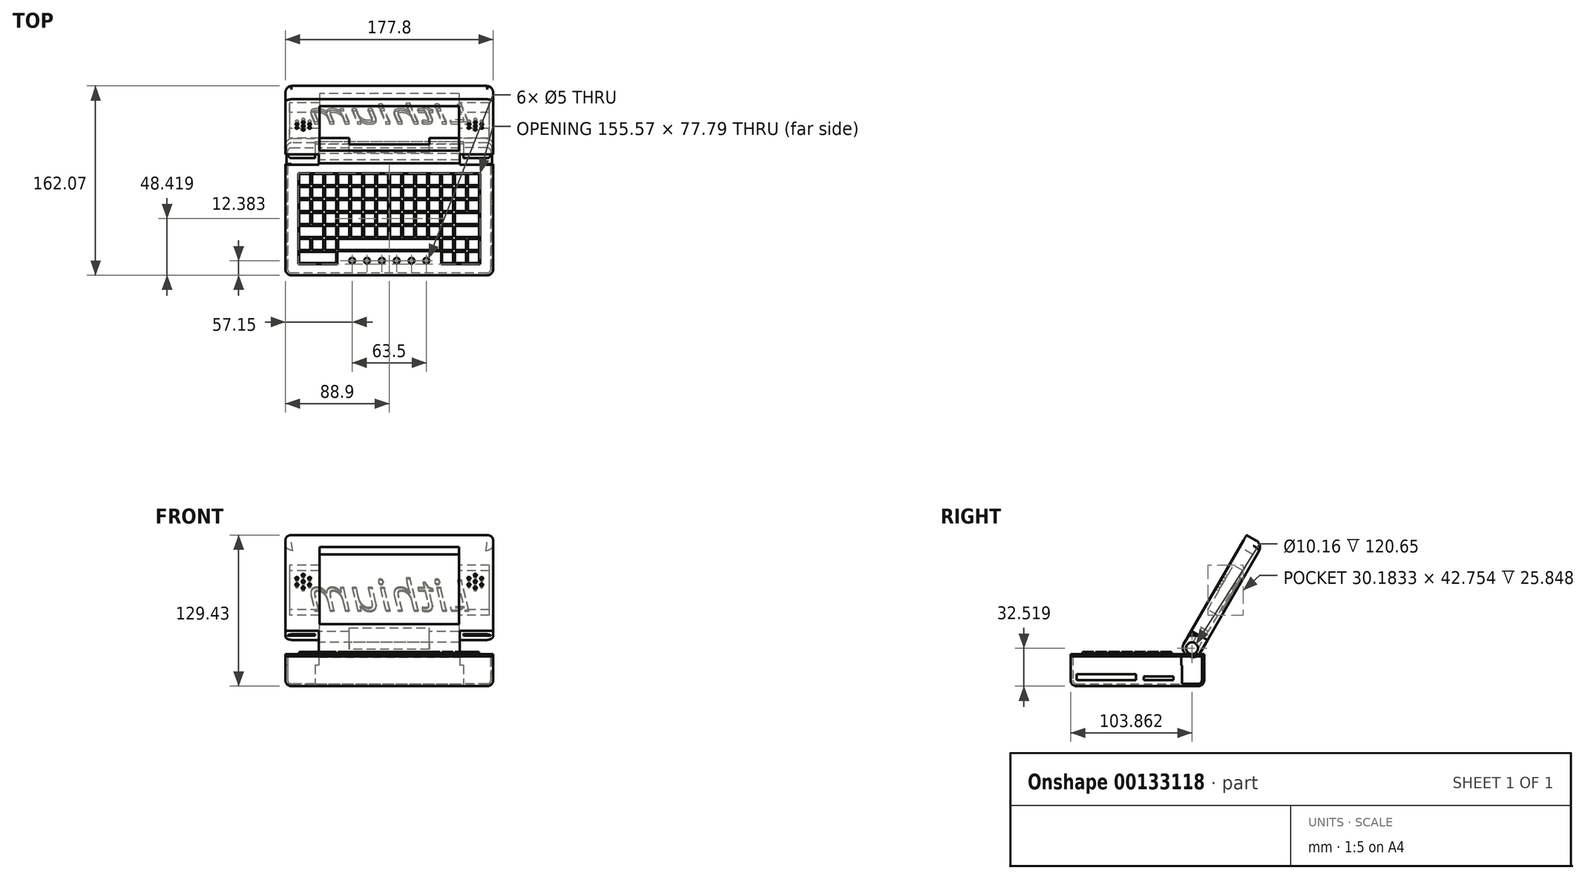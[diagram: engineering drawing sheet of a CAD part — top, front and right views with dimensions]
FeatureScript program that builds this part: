
annotation { "Feature Type Name" : "Feature", "Feature Type Description" : "" }
export const myFeature = defineFeature(function(context is Context, id is Id, definition is map)
    precondition{}
    {
        {
            var Q0;
            Q0=qCreatedBy(makeId("Top.planeOp"),FACE);
            var sketch = newSketch(context, id + "F0", { "sketchPlane" : qUnion([Q0])});
            skLineSegment(sketch, "E0.bottom", {"start": v(88.9, 57.15) * mm, "end": v(-88.9, 57.15) * mm});
            skLineSegment(sketch, "E0.top", {"start": v(88.9, -57.15) * mm, "end": v(-88.9, -57.15) * mm});
            skLineSegment(sketch, "E0.left", {"start": v(88.9, 57.15) * mm, "end": v(88.9, -57.15) * mm});
            skLineSegment(sketch, "E0.right", {"start": v(-88.9, 57.15) * mm, "end": v(-88.9, -57.15) * mm});
            skPoint(sketch, "E0.middle", {"position": v(0, 0) * mm});
            skSolve(sketch);
        }
        {
            var Q0;
            Q0 = qSketchRegion(id + "F0", true);
            extrude(context, id + "F1", {"entities" : qUnion([Q0]), "depth" : 25.4 * mm});
        }
        {
            var Q0;
            Q0=makeQuery(id+"F1.opExtrude","CAP_FACE",FACE,{"disambiguationData":[OSD([sQuery(id+"F0.wireOp",EDGE,"E0.bottom"),sQuery(id+"F0.wireOp",EDGE,"E0.top"),sQuery(id+"F0.wireOp",EDGE,"E0.left"),sQuery(id+"F0.wireOp",EDGE,"E0.right")])],"isStart":false});
            var sketch = newSketch(context, id + "F2", { "sketchPlane" : qUnion([Q0])});
            skLineSegment(sketch, "E1.bottom", {"start": v(-88.9, 57.15) * mm, "end": v(-63.5, 57.15) * mm});
            skLineSegment(sketch, "E1.top", {"start": v(-88.9, 38.1) * mm, "end": v(-63.5, 38.1) * mm});
            skLineSegment(sketch, "E1.left", {"start": v(-88.9, 57.15) * mm, "end": v(-88.9, 38.1) * mm});
            skLineSegment(sketch, "E1.right", {"start": v(-63.5, 57.15) * mm, "end": v(-63.5, 38.1) * mm});
            skLineSegment(sketch, "E2.MirrorCS", {"start": v(88.9, 57.15) * mm, "end": v(63.5, 57.15) * mm});
            skLineSegment(sketch, "E3.MirrorCS", {"start": v(88.9, 38.1) * mm, "end": v(63.5, 38.1) * mm});
            skLineSegment(sketch, "E4.MirrorCS", {"start": v(88.9, 57.15) * mm, "end": v(88.9, 38.1) * mm});
            skLineSegment(sketch, "E5.MirrorCS", {"start": v(63.5, 57.15) * mm, "end": v(63.5, 38.1) * mm});
            skSolve(sketch);
        }
        {
            var Q0;
            Q0 = qSketchRegion(id + "F2", true);
            extrude(context, id + "F3", {"entities" : qUnion([Q0]), "operationType" : NewBodyOperationType.ADD, "depth" : 19.05 * mm});
        }
        {
            var Q0;
            Q0=makeQuery(id+"F3.opExtrude","CAP_EDGE",EDGE,{"disambiguationData":[OSD([sQuery(id+"F2.wireOp",EDGE,"E3.MirrorCS")])],"isStart":false});
            var Q1;
            Q1=makeQuery(id+"F3.opExtrude","CAP_EDGE",EDGE,{"disambiguationData":[OSD([sQuery(id+"F2.wireOp",EDGE,"E2.MirrorCS")])],"isStart":false});
            var Q2;
            Q2=makeQuery(id+"F3.opExtrude","CAP_EDGE",EDGE,{"disambiguationData":[OSD([sQuery(id+"F2.wireOp",EDGE,"E1.bottom")])],"isStart":false});
            var Q3;
            Q3=makeQuery(id+"F3.opExtrude","CAP_EDGE",EDGE,{"disambiguationData":[OSD([sQuery(id+"F2.wireOp",EDGE,"E1.top")])],"isStart":false});
            fillet(context, id + "F4", {"entities" : qUnion([Q0, Q1, Q2, Q3]), "radius" : 9.52 * mm, "tangentPropagation" : true, "allowEdgeOverflow" : false});
        }
        {
            var Q0;
            Q0=makeQuery(id+"F4.opFillet","BLEND_EDGE",EDGE,{"blendedFrom":[makeQuery(id+"F3.opExtrude","CAP_EDGE",EDGE,{"disambiguationData":[OSD([sQuery(id+"F2.wireOp",EDGE,"E1.bottom")])],"isStart":false}),makeQuery(id+"F3.boolean.opBoolean","MERGE",FACE,{"derivedFrom":[makeQuery(id+"F1.opExtrude","SWEPT_FACE",FACE,{"disambiguationData":[OSD([sQuery(id+"F0.wireOp",EDGE,"E0.right")])]}),makeQuery(id+"F3.opExtrude","SWEPT_FACE",FACE,{"disambiguationData":[OSD([sQuery(id+"F2.wireOp",EDGE,"E1.left")])]})]})],"blendedInto":[makeQuery(id+"F3.boolean.opBoolean","MERGE",FACE,{"derivedFrom":[makeQuery(id+"F1.opExtrude","SWEPT_FACE",FACE,{"disambiguationData":[OSD([sQuery(id+"F0.wireOp",EDGE,"E0.right")])]}),makeQuery(id+"F3.opExtrude","SWEPT_FACE",FACE,{"disambiguationData":[OSD([sQuery(id+"F2.wireOp",EDGE,"E1.left")])]})]})]});
            var Q1;
            Q1=makeQuery(id+"F3.opExtrude","SWEPT_EDGE",EDGE,{"disambiguationData":[OSD([sQuery(id+"F0.wireOp",EDGE,"E0.right"),sQuery(id+"F2.wireOp",EDGE,"E1.top"),sQuery(id+"F2.wireOp",EDGE,"E1.left")])]});
            var Q2;
            Q2=makeQuery(id+"F1.opExtrude","SWEPT_EDGE",EDGE,{"disambiguationData":[OSD([sQuery(id+"F0.wireOp",EDGE,"E0.top"),sQuery(id+"F0.wireOp",EDGE,"E0.right")])]});
            var Q3;
            Q3=makeQuery(id+"F3.boolean.opBoolean","MERGE",EDGE,{"derivedFrom":[makeQuery(id+"F1.opExtrude","SWEPT_EDGE",EDGE,{"disambiguationData":[OSD([sQuery(id+"F0.wireOp",EDGE,"E0.bottom"),sQuery(id+"F0.wireOp",EDGE,"E0.right")])]}),makeQuery(id+"F3.opExtrude","SWEPT_EDGE",EDGE,{"disambiguationData":[OSD([sQuery(id+"F2.wireOp",EDGE,"E1.bottom"),sQuery(id+"F2.wireOp",EDGE,"E1.left")])]})]});
            var Q4;
            Q4=makeQuery(id+"F1.opExtrude","SWEPT_EDGE",EDGE,{"disambiguationData":[OSD([sQuery(id+"F0.wireOp",EDGE,"E0.top"),sQuery(id+"F0.wireOp",EDGE,"E0.left")])]});
            var Q5;
            Q5=makeQuery(id+"F3.boolean.opBoolean","MERGE",EDGE,{"derivedFrom":[makeQuery(id+"F1.opExtrude","SWEPT_EDGE",EDGE,{"disambiguationData":[OSD([sQuery(id+"F0.wireOp",EDGE,"E0.bottom"),sQuery(id+"F0.wireOp",EDGE,"E0.left")])]}),makeQuery(id+"F3.opExtrude","SWEPT_EDGE",EDGE,{"disambiguationData":[OSD([sQuery(id+"F2.wireOp",EDGE,"E2.MirrorCS"),sQuery(id+"F2.wireOp",EDGE,"E4.MirrorCS")])]})]});
            var Q6;
            Q6=makeQuery(id+"F1.opExtrude","CAP_FACE",FACE,{"disambiguationData":[OSD([sQuery(id+"F0.wireOp",EDGE,"E0.bottom"),sQuery(id+"F0.wireOp",EDGE,"E0.top"),sQuery(id+"F0.wireOp",EDGE,"E0.left"),sQuery(id+"F0.wireOp",EDGE,"E0.right")])],"isStart":true});
            fillet(context, id + "F5", {"entities" : qUnion([Q0, Q1, Q2, Q3, Q4, Q5, Q6]), "radius" : 5.08 * mm, "tangentPropagation" : true, "allowEdgeOverflow" : false});
        }
        {
            var Q0;
            Q0=makeQuery(id+"F1.opExtrude","CAP_FACE",FACE,{"disambiguationData":[OSD([sQuery(id+"F0.wireOp",EDGE,"E0.bottom"),sQuery(id+"F0.wireOp",EDGE,"E0.top"),sQuery(id+"F0.wireOp",EDGE,"E0.left"),sQuery(id+"F0.wireOp",EDGE,"E0.right")])],"isStart":false});
            shell(context, id + "F6", {"entities" : qUnion([Q0]), "thickness" : 2 * mm});
        }
        {
            var Q0;
            Q0=makeQuery(id+"F3.opExtrude","SWEPT_FACE",FACE,{"disambiguationData":[OSD([sQuery(id+"F2.wireOp",EDGE,"E5.MirrorCS")])]});
            var sketch = newSketch(context, id + "F7", { "sketchPlane" : qUnion([Q0])});
            skCircle(sketch, "E6", {"center": v(-47.63, 34.93) * mm, "radius": 7.94 * mm});
            skSolve(sketch);
        }
        {
            var Q0;
            Q0 = qSketchRegion(id + "F7", true);
            extrude(context, id + "F8", {"entities" : qUnion([Q0]), "operationType" : NewBodyOperationType.REMOVE, "oppositeDirection" : true, "depth" : 6.35 * mm});
        }
        {
            var Q0;
            Q0=makeQuery(id+"F3.opExtrude","SWEPT_FACE",FACE,{"disambiguationData":[OSD([sQuery(id+"F2.wireOp",EDGE,"E1.right")])]});
            var sketch = newSketch(context, id + "F9", { "sketchPlane" : qUnion([Q0])});
            skCircle(sketch, "E7", {"center": v(47.63, 34.93) * mm, "radius": 7.94 * mm});
            skSolve(sketch);
        }
        {
            var Q0;
            Q0 = qSketchRegion(id + "F9", true);
            extrude(context, id + "F10", {"entities" : qUnion([Q0]), "operationType" : NewBodyOperationType.REMOVE, "oppositeDirection" : true, "depth" : 6.35 * mm});
        }
        {
            var Q0;
            {var subQ0=sQuery(id+"F0.wireOp",EDGE,"E0.right");var subQ1=sQuery(id+"F0.wireOp",EDGE,"E0.left");var subQ2=sQuery(id+"F0.wireOp",EDGE,"E0.top");var subQ3=sQuery(id+"F0.wireOp",EDGE,"E0.bottom");Q0=makeQuery(id+"F6.opShell","OFFSET_FACE",FACE,{"disambiguationData":[OSD([subQ3,subQ2,subQ1,subQ0]),TDD([makeQuery(id+"F1.opExtrude","CAP_FACE",FACE,{"disambiguationData":[OSD([subQ3,subQ2,subQ1,subQ0])],"isStart":false})]),OD(0.0)]});}
            var sketch = newSketch(context, id + "F11", { "sketchPlane" : qUnion([Q0])});
            skLineSegment(sketch, "E8.bottom", {"start": v(-83.82, -57.15) * mm, "end": v(83.82, -57.15) * mm});
            skLineSegment(sketch, "E8.top", {"start": v(-88.9, 57.15) * mm, "end": v(88.9, 57.15) * mm});
            skLineSegment(sketch, "E8.left", {"start": v(-88.9, -52.07) * mm, "end": v(-88.9, 57.15) * mm});
            skLineSegment(sketch, "E8.right", {"start": v(88.9, -52.07) * mm, "end": v(88.9, 57.15) * mm});
            skPoint(sketch, "E9.visualSharp", {"position": v(-88.9, -57.15) * mm});
            skArc(sketch, "E9.filletArc", {"start": v(-88.9, -52.07) * mm, "mid": v(-87.41, -55.66) * mm, "end": v(-83.82, -57.15) * mm});
            skPoint(sketch, "E10.visualSharp", {"position": v(88.9, -57.15) * mm});
            skArc(sketch, "E10.filletArc", {"start": v(83.82, -57.15) * mm, "mid": v(87.41, -55.66) * mm, "end": v(88.9, -52.07) * mm});
            skLineSegment(sketch, "E11.top", {"start": v(-88.9, 38.1) * mm, "end": v(-63.5, 38.1) * mm});
            skLineSegment(sketch, "E11.right", {"start": v(-63.5, 57.15) * mm, "end": v(-63.5, 38.1) * mm});
            skLineSegment(sketch, "E12.MirrorCS", {"start": v(63.5, 57.15) * mm, "end": v(63.5, 38.1) * mm});
            skLineSegment(sketch, "E13.MirrorCS", {"start": v(88.9, 57.15) * mm, "end": v(88.9, 38.1) * mm});
            skLineSegment(sketch, "E14.MirrorCS", {"start": v(88.9, 38.1) * mm, "end": v(63.5, 38.1) * mm});
            skLineSegment(sketch, "E15.MirrorCS", {"start": v(88.9, 57.15) * mm, "end": v(63.5, 57.15) * mm});
            skSolve(sketch);
        }
        {
            var Q0;
            Q0 = qSketchRegion(id + "F11", true);
            extrude(context, id + "F12", {"entities" : qUnion([Q0]), "depth" : 2 * mm});
        }
        {
            var Q0;
            Q0=makeQuery(id+"F12.opExtrude","CAP_FACE",FACE,{"disambiguationData":[OSD([sQuery(id+"F11.wireOp",EDGE,"E8.bottom"),sQuery(id+"F11.wireOp",EDGE,"E8.top"),sQuery(id+"F11.wireOp",EDGE,"E8.left"),sQuery(id+"F11.wireOp",EDGE,"E8.right"),sQuery(id+"F11.wireOp",EDGE,"E9.filletArc"),sQuery(id+"F11.wireOp",EDGE,"E10.filletArc"),sQuery(id+"F11.wireOp",EDGE,"E13.MirrorCS"),sQuery(id+"F11.wireOp",EDGE,"E15.MirrorCS")])],"isStart":false});
            var sketch = newSketch(context, id + "F13", { "sketchPlane" : qUnion([Q0])});
            skLineSegment(sketch, "E16.bottom", {"start": v(-88.9, 57.15) * mm, "end": v(-63.5, 57.15) * mm});
            skLineSegment(sketch, "E16.top", {"start": v(-88.9, 38.1) * mm, "end": v(-63.5, 38.1) * mm});
            skLineSegment(sketch, "E16.left", {"start": v(-88.9, 57.15) * mm, "end": v(-88.9, 38.1) * mm});
            skLineSegment(sketch, "E16.right", {"start": v(-63.5, 57.15) * mm, "end": v(-63.5, 38.1) * mm});
            skLineSegment(sketch, "E17.MirrorCS", {"start": v(63.5, 57.15) * mm, "end": v(63.5, 38.1) * mm});
            skLineSegment(sketch, "E18.MirrorCS", {"start": v(88.9, 57.15) * mm, "end": v(88.9, 38.1) * mm});
            skLineSegment(sketch, "E19.MirrorCS", {"start": v(88.9, 38.1) * mm, "end": v(63.5, 38.1) * mm});
            skLineSegment(sketch, "E20.MirrorCS", {"start": v(88.9, 57.15) * mm, "end": v(63.5, 57.15) * mm});
            skSolve(sketch);
        }
        {
            var Q0;
            Q0 = qSketchRegion(id + "F13", true);
            extrude(context, id + "F14", {"entities" : qUnion([Q0]), "operationType" : NewBodyOperationType.REMOVE, "oppositeDirection" : true, "depth" : 25.4 * mm});
        }
        {
            var Q0;
            Q0=makeQuery(id+"F12.opExtrude","CAP_FACE",FACE,{"disambiguationData":[OSD([sQuery(id+"F11.wireOp",EDGE,"E8.bottom"),sQuery(id+"F11.wireOp",EDGE,"E8.top"),sQuery(id+"F11.wireOp",EDGE,"E8.left"),sQuery(id+"F11.wireOp",EDGE,"E8.right"),sQuery(id+"F11.wireOp",EDGE,"E9.filletArc"),sQuery(id+"F11.wireOp",EDGE,"E10.filletArc"),sQuery(id+"F11.wireOp",EDGE,"E13.MirrorCS"),sQuery(id+"F11.wireOp",EDGE,"E15.MirrorCS")])],"isStart":false});
            var sketch = newSketch(context, id + "F15", { "sketchPlane" : qUnion([Q0])});
            skLineSegment(sketch, "E21.bottom", {"start": v(-83.82, -57.15) * mm, "end": v(83.82, -57.15) * mm});
            skLineSegment(sketch, "E21.top", {"start": v(-88.9, 57.15) * mm, "end": v(88.9, 57.15) * mm});
            skLineSegment(sketch, "E21.left", {"start": v(-88.9, -52.07) * mm, "end": v(-88.9, 57.15) * mm});
            skLineSegment(sketch, "E21.right", {"start": v(88.9, -52.07) * mm, "end": v(88.9, 57.15) * mm});
            skPoint(sketch, "E22.visualSharp", {"position": v(-88.9, -57.15) * mm});
            skArc(sketch, "E22.filletArc", {"start": v(-88.9, -52.07) * mm, "mid": v(-87.41, -55.66) * mm, "end": v(-83.82, -57.15) * mm});
            skPoint(sketch, "E23.visualSharp", {"position": v(88.9, -57.15) * mm});
            skArc(sketch, "E23.filletArc", {"start": v(83.82, -57.15) * mm, "mid": v(87.41, -55.66) * mm, "end": v(88.9, -52.07) * mm});
            skSolve(sketch);
        }
        {
            var Q0;
            Q0 = qSketchRegion(id + "F15", true);
            extrude(context, id + "F16", {"entities" : qUnion([Q0]), "depth" : 15.88 * mm});
        }
        {
            var Q0;
            Q0=makeQuery(id+"F16.opExtrude","CAP_FACE",FACE,{"disambiguationData":[OSD([sQuery(id+"F15.wireOp",EDGE,"E21.bottom"),sQuery(id+"F15.wireOp",EDGE,"E21.top"),sQuery(id+"F15.wireOp",EDGE,"E21.left"),sQuery(id+"F15.wireOp",EDGE,"E21.right"),sQuery(id+"F15.wireOp",EDGE,"E22.filletArc"),sQuery(id+"F15.wireOp",EDGE,"E23.filletArc")])],"isStart":false});
            var sketch = newSketch(context, id + "F17", { "sketchPlane" : qUnion([Q0])});
            skLineSegment(sketch, "E24.bottom", {"start": v(-88.9, 57.15) * mm, "end": v(-60.32, 57.15) * mm});
            skLineSegment(sketch, "E24.top", {"start": v(-88.9, 37.46) * mm, "end": v(-60.32, 37.46) * mm});
            skLineSegment(sketch, "E24.left", {"start": v(-88.9, 57.15) * mm, "end": v(-88.9, 37.46) * mm});
            skLineSegment(sketch, "E24.right", {"start": v(-60.32, 57.15) * mm, "end": v(-60.32, 37.46) * mm});
            skLineSegment(sketch, "E25.MirrorCS", {"start": v(60.32, 57.15) * mm, "end": v(60.32, 37.46) * mm});
            skLineSegment(sketch, "E26.MirrorCS", {"start": v(88.9, 57.15) * mm, "end": v(88.9, 37.46) * mm});
            skLineSegment(sketch, "E27.MirrorCS", {"start": v(88.9, 37.46) * mm, "end": v(60.32, 37.46) * mm});
            skLineSegment(sketch, "E28.MirrorCS", {"start": v(88.9, 57.15) * mm, "end": v(60.32, 57.15) * mm});
            skSolve(sketch);
        }
        {
            var Q0;
            Q0 = qSketchRegion(id + "F17", true);
            extrude(context, id + "F18", {"entities" : qUnion([Q0]), "operationType" : NewBodyOperationType.REMOVE, "oppositeDirection" : true, "depth" : 25.4 * mm});
        }
        {
            var Q0;
            Q0=makeQuery(id+"F16.opExtrude","CAP_EDGE",EDGE,{"disambiguationData":[OSD([sQuery(id+"F15.wireOp",EDGE,"E21.top")])],"isStart":true});
            var Q1;
            Q1=makeQuery(id+"F16.opExtrude","CAP_EDGE",EDGE,{"disambiguationData":[OSD([sQuery(id+"F15.wireOp",EDGE,"E21.top")])],"isStart":false});
            var Q2;
            Q2=makeQuery(id+"F18.boolean.opBoolean","COPY",EDGE,{"derivedFrom":makeQuery(id+"F18.opExtrude","CAP_EDGE",EDGE,{"disambiguationData":[OSD([sQuery(id+"F17.wireOp",EDGE,"E27.MirrorCS")])],"isStart":true})});
            var Q3;
            Q3=makeQuery(id+"F16.opExtrude","CAP_EDGE",EDGE,{"disambiguationData":[OSD([sQuery(id+"F15.wireOp",EDGE,"E21.right")])],"isStart":false});
            var Q4;
            Q4=makeQuery(id+"F16.opExtrude","CAP_EDGE",EDGE,{"disambiguationData":[OSD([sQuery(id+"F15.wireOp",EDGE,"E23.filletArc")])],"isStart":false});
            var Q5;
            Q5=makeQuery(id+"F16.opExtrude","CAP_EDGE",EDGE,{"disambiguationData":[OSD([sQuery(id+"F15.wireOp",EDGE,"E21.bottom")])],"isStart":false});
            var Q6;
            Q6=makeQuery(id+"F16.opExtrude","CAP_EDGE",EDGE,{"disambiguationData":[OSD([sQuery(id+"F15.wireOp",EDGE,"E22.filletArc")])],"isStart":false});
            var Q7;
            Q7=makeQuery(id+"F16.opExtrude","CAP_EDGE",EDGE,{"disambiguationData":[OSD([sQuery(id+"F15.wireOp",EDGE,"E21.left")])],"isStart":false});
            var Q8;
            Q8=makeQuery(id+"F18.boolean.opBoolean","COPY",EDGE,{"derivedFrom":makeQuery(id+"F18.opExtrude","CAP_EDGE",EDGE,{"disambiguationData":[OSD([sQuery(id+"F17.wireOp",EDGE,"E24.top")])],"isStart":true})});
            fillet(context, id + "F19", {"entities" : qUnion([Q0, Q1, Q2, Q3, Q4, Q5, Q6, Q7, Q8]), "radius" : 6.35 * mm, "tangentPropagation" : true, "allowEdgeOverflow" : false});
        }
        {
            var Q0;
            Q0=qCreatedBy(makeId("Top.planeOp"),FACE);
            cPlane(context, id + "F20", {"entities" : qUnion([Q0]), "cplaneType" : CPlaneType.OFFSET, "offset" : 34.92 * mm, "width" : 152.4 * mm, "height" : 152.4 * mm});
        }
        {
            var Q0;
            Q0=qCreatedBy(id+"F20.planeOp",FACE);
            var sketch = newSketch(context, id + "F21", { "sketchPlane" : qUnion([Q0])});
            skLineSegment(sketch, "E29", {"start": v(-88.65, 47.63) * mm, "end": v(89.15, 47.63) * mm});
            skSolve(sketch);
        }
        {
            var Q0;
            Q0=makeQuery(id+"F12.opExtrude","CAP_FACE",FACE,{"disambiguationData":[OSD([sQuery(id+"F11.wireOp",EDGE,"E8.bottom"),sQuery(id+"F11.wireOp",EDGE,"E8.top"),sQuery(id+"F11.wireOp",EDGE,"E8.left"),sQuery(id+"F11.wireOp",EDGE,"E8.right"),sQuery(id+"F11.wireOp",EDGE,"E9.filletArc"),sQuery(id+"F11.wireOp",EDGE,"E10.filletArc"),sQuery(id+"F11.wireOp",EDGE,"E13.MirrorCS"),sQuery(id+"F11.wireOp",EDGE,"E15.MirrorCS")])],"isStart":false});
            var sketch = newSketch(context, id + "F22", { "sketchPlane" : qUnion([Q0])});
            skLineSegment(sketch, "E30.bottom", {"start": v(77.79, 30.16) * mm, "end": v(-77.79, 30.16) * mm});
            skLineSegment(sketch, "E30.top", {"start": v(77.79, -36.51) * mm, "end": v(-77.79, -36.51) * mm});
            skLineSegment(sketch, "E30.left", {"start": v(77.79, 30.16) * mm, "end": v(77.79, -36.51) * mm});
            skLineSegment(sketch, "E30.right", {"start": v(-77.79, 30.16) * mm, "end": v(-77.79, -36.51) * mm});
            skPoint(sketch, "E30.middle", {"position": v(0, -3.18) * mm});
            skLineSegment(sketch, "E31.bottom", {"start": v(77.79, -36.51) * mm, "end": v(44.45, -36.51) * mm});
            skLineSegment(sketch, "E31.top", {"start": v(77.79, -47.62) * mm, "end": v(44.45, -47.63) * mm});
            skLineSegment(sketch, "E31.left", {"start": v(77.79, -36.51) * mm, "end": v(77.79, -47.62) * mm});
            skLineSegment(sketch, "E31.right", {"start": v(44.45, -36.51) * mm, "end": v(44.45, -47.63) * mm});
            skLineSegment(sketch, "E32.MirrorCS", {"start": v(-77.79, -36.51) * mm, "end": v(-44.45, -36.51) * mm});
            skLineSegment(sketch, "E33.MirrorCS", {"start": v(-77.79, -47.62) * mm, "end": v(-44.45, -47.63) * mm});
            skLineSegment(sketch, "E34.MirrorCS", {"start": v(-44.45, -36.51) * mm, "end": v(-44.45, -47.63) * mm});
            skLineSegment(sketch, "E35.MirrorCS", {"start": v(-77.79, -36.51) * mm, "end": v(-77.79, -47.62) * mm});
            skSolve(sketch);
        }
        {
            var Q0;
            Q0 = qSketchRegion(id + "F22", true);
            extrude(context, id + "F23", {"entities" : qUnion([Q0]), "operationType" : NewBodyOperationType.REMOVE, "oppositeDirection" : true, "depth" : 25.4 * mm});
        }
        {
            var Q0;
            Q0=makeQuery(id+"F16.opExtrude","CAP_FACE",FACE,{"disambiguationData":[OSD([sQuery(id+"F15.wireOp",EDGE,"E21.bottom"),sQuery(id+"F15.wireOp",EDGE,"E21.top"),sQuery(id+"F15.wireOp",EDGE,"E21.left"),sQuery(id+"F15.wireOp",EDGE,"E21.right"),sQuery(id+"F15.wireOp",EDGE,"E22.filletArc"),sQuery(id+"F15.wireOp",EDGE,"E23.filletArc")])],"isStart":true});
            var sketch = newSketch(context, id + "F24", { "sketchPlane" : qUnion([Q0])});
            skLineSegment(sketch, "E36.bottom", {"start": v(59.7, 45.27) * mm, "end": v(-59.7, 45.27) * mm});
            skLineSegment(sketch, "E36.top", {"start": v(59.7, -30.93) * mm, "end": v(-59.69, -30.93) * mm});
            skLineSegment(sketch, "E36.left", {"start": v(59.7, 45.27) * mm, "end": v(59.7, -30.93) * mm});
            skLineSegment(sketch, "E36.right", {"start": v(-59.7, 45.27) * mm, "end": v(-59.69, -30.93) * mm});
            skPoint(sketch, "E36.middle", {"position": v(0, 7.17) * mm});
            skSolve(sketch);
        }
        {
            var Q0;
            Q0 = qSketchRegion(id + "F24", true);
            extrude(context, id + "F25", {"entities" : qUnion([Q0]), "operationType" : NewBodyOperationType.REMOVE, "oppositeDirection" : true, "depth" : 12.7 * mm});
        }
        {
            var Q0;
            Q0=makeQuery(id+"F16.opExtrude","SWEPT_BODY",BODY,{"disambiguationData":[OSD([sQuery(id+"F15.wireOp",EDGE,"E21.bottom"),sQuery(id+"F15.wireOp",EDGE,"E21.top"),sQuery(id+"F15.wireOp",EDGE,"E21.left"),sQuery(id+"F15.wireOp",EDGE,"E21.right"),sQuery(id+"F15.wireOp",EDGE,"E22.filletArc"),sQuery(id+"F15.wireOp",EDGE,"E23.filletArc")])]});
            var Q1;
            Q1=sQuery(id+"F21.wireOp",EDGE,"E29");
            transform(context, id + "F26", {"entities" : qUnion([Q0]), "transformType" : TransformType.ROTATION, "transformAxis" : qUnion([Q1]), "angle" : 90 * degree, "oppositeDirection" : true, "makeCopy" : false});
        }
        {
            var Q0;
            Q0=makeQuery(id+"F25.boolean.opBoolean","COPY",FACE,{"derivedFrom":makeQuery(id+"F25.opExtrude","CAP_FACE",FACE,{"disambiguationData":[OSD([sQuery(id+"F24.wireOp",EDGE,"E36.bottom"),sQuery(id+"F24.wireOp",EDGE,"E36.top"),sQuery(id+"F24.wireOp",EDGE,"E36.left"),sQuery(id+"F24.wireOp",EDGE,"E36.right")])],"isStart":false})});
            var sketch = newSketch(context, id + "F27", { "sketchPlane" : qUnion([Q0])});
            skLineSegment(sketch, "E37.bottom", {"start": v(85.54, 111.66) * mm, "end": v(-85.54, 111.66) * mm});
            skLineSegment(sketch, "E37.top", {"start": v(85.54, 67.79) * mm, "end": v(-85.54, 67.79) * mm});
            skLineSegment(sketch, "E37.left", {"start": v(85.54, 111.66) * mm, "end": v(85.54, 67.79) * mm});
            skLineSegment(sketch, "E37.right", {"start": v(-85.54, 111.66) * mm, "end": v(-85.54, 67.79) * mm});
            skPoint(sketch, "E37.middle", {"position": v(0, 89.72) * mm});
            skPoint(sketch, "E37.middle.positionSnap0", {"position": v(-59.7, 89.72) * mm});
            skPoint(sketch, "E37.middle.positionSnap1", {"position": v(0, 127.82) * mm});
            skPoint(sketch, "E37.centerSnap0", {"position": v(-59.7, 89.72) * mm});
            skPoint(sketch, "E37.centerSnap1", {"position": v(0, 127.82) * mm});
            skSolve(sketch);
        }
        {
            var Q0;
            Q0 = qSketchRegion(id + "F27", true);
            extrude(context, id + "F28", {"entities" : qUnion([Q0]), "operationType" : NewBodyOperationType.REMOVE, "depth" : 9.52 * mm});
        }
        {
            var Q0;
            Q0=makeQuery(id+"F16.opExtrude","CAP_FACE",FACE,{"disambiguationData":[OSD([sQuery(id+"F15.wireOp",EDGE,"E21.bottom"),sQuery(id+"F15.wireOp",EDGE,"E21.top"),sQuery(id+"F15.wireOp",EDGE,"E21.left"),sQuery(id+"F15.wireOp",EDGE,"E21.right"),sQuery(id+"F15.wireOp",EDGE,"E22.filletArc"),sQuery(id+"F15.wireOp",EDGE,"E23.filletArc")])],"isStart":true});
            var sketch = newSketch(context, id + "F29", { "sketchPlane" : qUnion([Q0])});
            skCircle(sketch, "E38", {"center": v(-73.63, 93.85) * mm, "radius": 1.27 * mm});
            skCircle(sketch, "E39", {"center": v(-73.63, 100.14) * mm, "radius": 1.27 * mm});
            skCircle(sketch, "E40.1.0", {"center": v(-79.08, 97) * mm, "radius": 1.27 * mm});
            skCircle(sketch, "E40.2.0", {"center": v(-79.08, 90.7) * mm, "radius": 1.27 * mm});
            skCircle(sketch, "E40.3.0", {"center": v(-73.63, 87.55) * mm, "radius": 1.27 * mm});
            skCircle(sketch, "E40.4.0", {"center": v(-68.17, 90.7) * mm, "radius": 1.27 * mm});
            skCircle(sketch, "E40.5.0", {"center": v(-68.17, 97) * mm, "radius": 1.27 * mm});
            skCircle(sketch, "E41.MirrorC", {"center": v(73.63, 93.85) * mm, "radius": 1.27 * mm});
            skCircle(sketch, "E42.MirrorC", {"center": v(73.63, 100.14) * mm, "radius": 1.27 * mm});
            skCircle(sketch, "E43.MirrorC", {"center": v(68.17, 97) * mm, "radius": 1.27 * mm});
            skCircle(sketch, "E44.MirrorC", {"center": v(79.08, 97) * mm, "radius": 1.27 * mm});
            skCircle(sketch, "E45.MirrorC", {"center": v(79.08, 90.7) * mm, "radius": 1.27 * mm});
            skCircle(sketch, "E46.MirrorC", {"center": v(68.17, 90.7) * mm, "radius": 1.27 * mm});
            skCircle(sketch, "E47.MirrorC", {"center": v(73.63, 87.55) * mm, "radius": 1.27 * mm});
            skSolve(sketch);
        }
        {
            var Q0;
            Q0 = qSketchRegion(id + "F29", true);
            extrude(context, id + "F30", {"entities" : qUnion([Q0]), "operationType" : NewBodyOperationType.REMOVE, "oppositeDirection" : true, "depth" : 12.7 * mm});
        }
        {
            var Q0;
            Q0=makeQuery(id+"F18.boolean.opBoolean","COPY",FACE,{"derivedFrom":makeQuery(id+"F18.opExtrude","SWEPT_FACE",FACE,{"disambiguationData":[OSD([sQuery(id+"F17.wireOp",EDGE,"E24.right")])]})});
            var sketch = newSketch(context, id + "F31", { "sketchPlane" : qUnion([Q0])});
            skCircle(sketch, "E48", {"center": v(-48.04, 32.39) * mm, "radius": 5.08 * mm});
            skPoint(sketch, "E48.centerSnap0", {"position": v(-48.04, 25.4) * mm});
            skSolve(sketch);
        }
        {
            var Q0;
            Q0 = qSketchRegion(id + "F31", true);
            extrude(context, id + "F32", {"entities" : qUnion([Q0]), "operationType" : NewBodyOperationType.REMOVE, "oppositeDirection" : true, "depth" : 203.2 * mm});
        }
        {
            var Q0;
            Q0=makeQuery(id+"F25.boolean.opBoolean","COPY",FACE,{"derivedFrom":makeQuery(id+"F25.opExtrude","SWEPT_FACE",FACE,{"disambiguationData":[OSD([sQuery(id+"F24.wireOp",EDGE,"E36.top")])]})});
            var sketch = newSketch(context, id + "F33", { "sketchPlane" : qUnion([Q0])});
            skLineSegment(sketch, "E49.bottom", {"start": v(-34.3, 52.8) * mm, "end": v(34.3, 52.8) * mm});
            skLineSegment(sketch, "E49.top", {"start": v(-34.3, 46.45) * mm, "end": v(34.3, 46.45) * mm});
            skLineSegment(sketch, "E49.left", {"start": v(-34.3, 52.8) * mm, "end": v(-34.3, 46.45) * mm});
            skLineSegment(sketch, "E49.right", {"start": v(34.3, 52.8) * mm, "end": v(34.3, 46.45) * mm});
            skSolve(sketch);
        }
        {
            var Q0;
            Q0 = qSketchRegion(id + "F33", true);
            extrude(context, id + "F34", {"entities" : qUnion([Q0]), "operationType" : NewBodyOperationType.REMOVE, "oppositeDirection" : true, "depth" : 19.05 * mm});
        }
        {
            var Q0;
            Q0=makeQuery(id+"F16.opExtrude","CAP_FACE",FACE,{"disambiguationData":[OSD([sQuery(id+"F15.wireOp",EDGE,"E21.bottom"),sQuery(id+"F15.wireOp",EDGE,"E21.top"),sQuery(id+"F15.wireOp",EDGE,"E21.left"),sQuery(id+"F15.wireOp",EDGE,"E21.right"),sQuery(id+"F15.wireOp",EDGE,"E22.filletArc"),sQuery(id+"F15.wireOp",EDGE,"E23.filletArc")])],"isStart":false});
            var sketch = newSketch(context, id + "F35", { "sketchPlane" : qUnion([Q0])});
            skText(sketch, "E50", { "text": "Lithium", "fontName": "OpenSans-Italic.ttf"});
            const initialGuessF35  = {"E50": [-0.06985, 0.07356, 1, 0, 0.0301]};
            skSetInitialGuess(sketch, initialGuessF35);
            skSolve(sketch);
        }
        {
            var Q0;
            Q0 = qSketchRegion(id + "F35", true);
            extrude(context, id + "F36", {"entities" : qUnion([Q0]), "operationType" : NewBodyOperationType.REMOVE, "oppositeDirection" : true, "depth" : 2 * mm});
        }
        {
            var Q0;
            Q0=makeQuery(id+"F16.opExtrude","SWEPT_BODY",BODY,{"disambiguationData":[OSD([sQuery(id+"F15.wireOp",EDGE,"E21.bottom"),sQuery(id+"F15.wireOp",EDGE,"E21.top"),sQuery(id+"F15.wireOp",EDGE,"E21.left"),sQuery(id+"F15.wireOp",EDGE,"E21.right"),sQuery(id+"F15.wireOp",EDGE,"E22.filletArc"),sQuery(id+"F15.wireOp",EDGE,"E23.filletArc")])]});
            var Q1;
            Q1=sQuery(id+"F21.wireOp",EDGE,"E29");
            transform(context, id + "F37", {"entities" : qUnion([Q0]), "transformType" : TransformType.ROTATION, "transformAxis" : qUnion([Q1]), "angle" : 30 * degree, "oppositeDirection" : true, "makeCopy" : false});
        }
        {
            var Q0;
            Q0=makeQuery(id+"F12.opExtrude","CAP_FACE",FACE,{"disambiguationData":[OSD([sQuery(id+"F11.wireOp",EDGE,"E8.bottom"),sQuery(id+"F11.wireOp",EDGE,"E8.top"),sQuery(id+"F11.wireOp",EDGE,"E8.left"),sQuery(id+"F11.wireOp",EDGE,"E8.right"),sQuery(id+"F11.wireOp",EDGE,"E9.filletArc"),sQuery(id+"F11.wireOp",EDGE,"E10.filletArc"),sQuery(id+"F11.wireOp",EDGE,"E13.MirrorCS"),sQuery(id+"F11.wireOp",EDGE,"E15.MirrorCS")])],"isStart":false});
            var sketch = newSketch(context, id + "F38", { "sketchPlane" : qUnion([Q0])});
            skCircle(sketch, "E51", {"center": v(-31.75, -44.77) * mm, "radius": 2.5 * mm});
            skCircle(sketch, "E52.1.0.0", {"center": v(-19.05, -44.77) * mm, "radius": 2.5 * mm});
            skCircle(sketch, "E52.2.0.0", {"center": v(-6.35, -44.77) * mm, "radius": 2.5 * mm});
            skCircle(sketch, "E52.3.0.0", {"center": v(6.35, -44.77) * mm, "radius": 2.5 * mm});
            skCircle(sketch, "E52.4.0.0", {"center": v(19.05, -44.77) * mm, "radius": 2.5 * mm});
            skCircle(sketch, "E52.5.0.0", {"center": v(31.75, -44.77) * mm, "radius": 2.5 * mm});
            skLineSegment(sketch, "E52.direction1", {"start": v(-31.75, -44.77) * mm, "end": v(-19.05, -44.77) * mm, "construction": true});
            skSolve(sketch);
        }
        {
            var Q0;
            Q0 = qSketchRegion(id + "F38", true);
            extrude(context, id + "F39", {"entities" : qUnion([Q0]), "operationType" : NewBodyOperationType.REMOVE, "oppositeDirection" : true, "depth" : 25.4 * mm});
        }
        {
            var Q0;
            Q0=makeQuery(id+"F3.boolean.opBoolean","MERGE",FACE,{"derivedFrom":[makeQuery(id+"F1.opExtrude","SWEPT_FACE",FACE,{"disambiguationData":[OSD([sQuery(id+"F0.wireOp",EDGE,"E0.left")])]}),makeQuery(id+"F3.opExtrude","SWEPT_FACE",FACE,{"disambiguationData":[OSD([sQuery(id+"F2.wireOp",EDGE,"E4.MirrorCS")])]})]});
            var sketch = newSketch(context, id + "F40", { "sketchPlane" : qUnion([Q0])});
            skLineSegment(sketch, "E53.bottom", {"start": v(-52.07, 5.08) * mm, "end": v(-1.27, 5.08) * mm});
            skLineSegment(sketch, "E53.top", {"start": v(-52.07, 10.16) * mm, "end": v(-1.27, 10.16) * mm});
            skLineSegment(sketch, "E53.left", {"start": v(-52.07, 5.08) * mm, "end": v(-52.07, 10.16) * mm});
            skLineSegment(sketch, "E53.right", {"start": v(-1.27, 5.08) * mm, "end": v(-1.27, 10.16) * mm});
            skLineSegment(sketch, "E54.bottom", {"start": v(52.07, 5.08) * mm, "end": v(41.91, 5.08) * mm});
            skLineSegment(sketch, "E54.top", {"start": v(52.07, 10.16) * mm, "end": v(41.91, 10.16) * mm});
            skLineSegment(sketch, "E54.left", {"start": v(52.07, 5.08) * mm, "end": v(52.07, 10.16) * mm});
            skLineSegment(sketch, "E54.right", {"start": v(41.91, 5.08) * mm, "end": v(41.91, 10.16) * mm});
            skLineSegment(sketch, "E55.bottom", {"start": v(5.52, 5.08) * mm, "end": v(30.92, 5.08) * mm});
            skLineSegment(sketch, "E55.top", {"start": v(5.52, 8.26) * mm, "end": v(30.92, 8.26) * mm});
            skLineSegment(sketch, "E55.left", {"start": v(5.52, 5.08) * mm, "end": v(5.52, 8.26) * mm});
            skLineSegment(sketch, "E55.right", {"start": v(30.92, 5.08) * mm, "end": v(30.92, 8.26) * mm});
            skSolve(sketch);
        }
        {
            var Q0;
            Q0 = qSketchRegion(id + "F40", true);
            extrude(context, id + "F41", {"entities" : qUnion([Q0]), "operationType" : NewBodyOperationType.REMOVE, "oppositeDirection" : true, "depth" : 25.4 * mm});
        }
        {
            var Q0;
            Q0=makeQuery(id+"F3.boolean.opBoolean","MERGE",FACE,{"derivedFrom":[makeQuery(id+"F1.opExtrude","SWEPT_FACE",FACE,{"disambiguationData":[OSD([sQuery(id+"F0.wireOp",EDGE,"E0.right")])]}),makeQuery(id+"F3.opExtrude","SWEPT_FACE",FACE,{"disambiguationData":[OSD([sQuery(id+"F2.wireOp",EDGE,"E1.left")])]})]});
            var sketch = newSketch(context, id + "F42", { "sketchPlane" : qUnion([Q0])});
            skLineSegment(sketch, "E56.bottom", {"start": v(-43.82, 19.05) * mm, "end": v(-51.44, 19.05) * mm});
            skLineSegment(sketch, "E56.top", {"start": v(-43.82, 11.43) * mm, "end": v(-51.44, 11.43) * mm});
            skLineSegment(sketch, "E56.left", {"start": v(-43.82, 19.05) * mm, "end": v(-43.82, 11.43) * mm});
            skLineSegment(sketch, "E56.right", {"start": v(-51.44, 19.05) * mm, "end": v(-51.44, 11.43) * mm});
            skPoint(sketch, "E56.middle", {"position": v(-47.63, 15.24) * mm});
            skPoint(sketch, "E56.middle.positionSnap0", {"position": v(-47.63, 39.37) * mm});
            skPoint(sketch, "E56.middle.positionSnap1", {"position": v(52.07, 15.24) * mm});
            skPoint(sketch, "E56.centerSnap0", {"position": v(-47.63, 39.37) * mm});
            skPoint(sketch, "E56.centerSnap1", {"position": v(52.07, 15.24) * mm});
            skSolve(sketch);
        }
        {
            var Q0;
            Q0 = qSketchRegion(id + "F42", true);
            extrude(context, id + "F43", {"entities" : qUnion([Q0]), "operationType" : NewBodyOperationType.REMOVE, "oppositeDirection" : true, "depth" : 25.4 * mm});
        }
        {
            var Q0;
            {var subQ0=sQuery(id+"F0.wireOp",EDGE,"E0.right");var subQ1=sQuery(id+"F0.wireOp",EDGE,"E0.left");var subQ2=sQuery(id+"F0.wireOp",EDGE,"E0.top");var subQ3=sQuery(id+"F0.wireOp",EDGE,"E0.bottom");Q0=makeQuery(id+"F6.opShell","OFFSET_FACE",FACE,{"disambiguationData":[OSD([subQ3,subQ2,subQ1,subQ0]),TDD([makeQuery(id+"F1.opExtrude","CAP_FACE",FACE,{"disambiguationData":[OSD([subQ3,subQ2,subQ1,subQ0])],"isStart":false})]),OD(0.0)]});}
            var sketch = newSketch(context, id + "F44", { "sketchPlane" : qUnion([Q0])});
            skLineSegment(sketch, "E57.bottom", {"start": v(-77, 29.37) * mm, "end": v(-67.47, 29.37) * mm});
            skLineSegment(sketch, "E57.top", {"start": v(-77, 19.84) * mm, "end": v(-67.47, 19.84) * mm});
            skLineSegment(sketch, "E57.left", {"start": v(-77, 29.37) * mm, "end": v(-77, 19.84) * mm});
            skLineSegment(sketch, "E57.right", {"start": v(-67.47, 29.37) * mm, "end": v(-67.47, 19.84) * mm});
            skLineSegment(sketch, "E58.0.1.0", {"start": v(-77, 8.73) * mm, "end": v(-67.47, 8.73) * mm});
            skLineSegment(sketch, "E58.0.1.1", {"start": v(-77, 18.26) * mm, "end": v(-67.47, 18.26) * mm});
            skLineSegment(sketch, "E58.0.1.2", {"start": v(-67.47, 18.26) * mm, "end": v(-67.47, 8.73) * mm});
            skLineSegment(sketch, "E58.0.1.3", {"start": v(-77, 18.26) * mm, "end": v(-77, 8.73) * mm});
            skLineSegment(sketch, "E58.0.2.0", {"start": v(-77, -2.38) * mm, "end": v(-67.47, -2.38) * mm});
            skLineSegment(sketch, "E58.0.2.1", {"start": v(-77, 7.14) * mm, "end": v(-67.47, 7.14) * mm});
            skLineSegment(sketch, "E58.0.2.2", {"start": v(-67.47, 7.14) * mm, "end": v(-67.47, -2.38) * mm});
            skLineSegment(sketch, "E58.0.2.3", {"start": v(-77, 7.14) * mm, "end": v(-77, -2.38) * mm});
            skLineSegment(sketch, "E58.0.3.0", {"start": v(-77, -13.5) * mm, "end": v(-67.47, -13.5) * mm});
            skLineSegment(sketch, "E58.0.3.1", {"start": v(-77, -3.97) * mm, "end": v(-67.47, -3.97) * mm});
            skLineSegment(sketch, "E58.0.3.2", {"start": v(-67.47, -3.97) * mm, "end": v(-67.47, -13.5) * mm});
            skLineSegment(sketch, "E58.0.3.3", {"start": v(-77, -3.97) * mm, "end": v(-77, -13.5) * mm});
            skLineSegment(sketch, "E58.0.4.0", {"start": v(-77, -24.6) * mm, "end": v(-67.47, -24.6) * mm});
            skLineSegment(sketch, "E58.0.4.1", {"start": v(-77, -15.08) * mm, "end": v(-67.47, -15.08) * mm});
            skLineSegment(sketch, "E58.0.4.2", {"start": v(-67.47, -15.08) * mm, "end": v(-67.47, -24.6) * mm});
            skLineSegment(sketch, "E58.0.4.3", {"start": v(-77, -15.08) * mm, "end": v(-77, -24.6) * mm});
            skLineSegment(sketch, "E58.0.5.0", {"start": v(-77, -35.72) * mm, "end": v(-67.47, -35.72) * mm});
            skLineSegment(sketch, "E58.0.5.1", {"start": v(-77, -26.2) * mm, "end": v(-67.47, -26.2) * mm});
            skLineSegment(sketch, "E58.0.5.2", {"start": v(-67.47, -26.2) * mm, "end": v(-67.47, -35.72) * mm});
            skLineSegment(sketch, "E58.0.5.3", {"start": v(-77, -26.2) * mm, "end": v(-77, -35.72) * mm});
            skLineSegment(sketch, "E58.1.0.0", {"start": v(-65.88, 19.84) * mm, "end": v(-56.36, 19.84) * mm});
            skLineSegment(sketch, "E58.1.0.1", {"start": v(-65.88, 29.37) * mm, "end": v(-56.36, 29.37) * mm});
            skLineSegment(sketch, "E58.1.0.2", {"start": v(-56.36, 29.37) * mm, "end": v(-56.36, 19.84) * mm});
            skLineSegment(sketch, "E58.1.0.3", {"start": v(-65.88, 29.37) * mm, "end": v(-65.88, 19.84) * mm});
            skLineSegment(sketch, "E58.1.1.0", {"start": v(-65.88, 8.73) * mm, "end": v(-56.36, 8.73) * mm});
            skLineSegment(sketch, "E58.1.1.1", {"start": v(-65.88, 18.26) * mm, "end": v(-56.36, 18.26) * mm});
            skLineSegment(sketch, "E58.1.1.2", {"start": v(-56.36, 18.26) * mm, "end": v(-56.36, 8.73) * mm});
            skLineSegment(sketch, "E58.1.1.3", {"start": v(-65.88, 18.26) * mm, "end": v(-65.88, 8.73) * mm});
            skLineSegment(sketch, "E58.1.2.0", {"start": v(-65.88, -2.38) * mm, "end": v(-56.36, -2.38) * mm});
            skLineSegment(sketch, "E58.1.2.1", {"start": v(-65.88, 7.14) * mm, "end": v(-56.36, 7.14) * mm});
            skLineSegment(sketch, "E58.1.2.2", {"start": v(-56.36, 7.14) * mm, "end": v(-56.36, -2.38) * mm});
            skLineSegment(sketch, "E58.1.2.3", {"start": v(-65.88, 7.14) * mm, "end": v(-65.88, -2.38) * mm});
            skLineSegment(sketch, "E58.1.3.0", {"start": v(-65.88, -13.5) * mm, "end": v(-56.36, -13.5) * mm});
            skLineSegment(sketch, "E58.1.3.1", {"start": v(-65.88, -3.97) * mm, "end": v(-56.36, -3.97) * mm});
            skLineSegment(sketch, "E58.1.3.2", {"start": v(-56.36, -3.97) * mm, "end": v(-56.36, -13.5) * mm});
            skLineSegment(sketch, "E58.1.3.3", {"start": v(-65.88, -3.97) * mm, "end": v(-65.88, -13.5) * mm});
            skLineSegment(sketch, "E58.1.4.0", {"start": v(-65.88, -24.6) * mm, "end": v(-56.36, -24.6) * mm});
            skLineSegment(sketch, "E58.1.4.1", {"start": v(-65.88, -15.08) * mm, "end": v(-56.36, -15.08) * mm});
            skLineSegment(sketch, "E58.1.4.2", {"start": v(-56.36, -15.08) * mm, "end": v(-56.36, -24.6) * mm});
            skLineSegment(sketch, "E58.1.4.3", {"start": v(-65.88, -15.08) * mm, "end": v(-65.88, -24.6) * mm});
            skLineSegment(sketch, "E58.1.5.0", {"start": v(-65.88, -35.72) * mm, "end": v(-56.36, -35.72) * mm});
            skLineSegment(sketch, "E58.1.5.1", {"start": v(-65.88, -26.2) * mm, "end": v(-56.36, -26.2) * mm});
            skLineSegment(sketch, "E58.1.5.2", {"start": v(-56.36, -26.2) * mm, "end": v(-56.36, -35.72) * mm});
            skLineSegment(sketch, "E58.1.5.3", {"start": v(-65.88, -26.2) * mm, "end": v(-65.88, -35.72) * mm});
            skLineSegment(sketch, "E58.2.0.0", {"start": v(-54.77, 19.84) * mm, "end": v(-45.24, 19.84) * mm});
            skLineSegment(sketch, "E58.2.0.1", {"start": v(-54.77, 29.37) * mm, "end": v(-45.24, 29.37) * mm});
            skLineSegment(sketch, "E58.2.0.2", {"start": v(-45.24, 29.37) * mm, "end": v(-45.24, 19.84) * mm});
            skLineSegment(sketch, "E58.2.0.3", {"start": v(-54.77, 29.37) * mm, "end": v(-54.77, 19.84) * mm});
            skLineSegment(sketch, "E58.2.1.0", {"start": v(-54.77, 8.73) * mm, "end": v(-45.24, 8.73) * mm});
            skLineSegment(sketch, "E58.2.1.1", {"start": v(-54.77, 18.26) * mm, "end": v(-45.24, 18.26) * mm});
            skLineSegment(sketch, "E58.2.1.2", {"start": v(-45.24, 18.26) * mm, "end": v(-45.24, 8.73) * mm});
            skLineSegment(sketch, "E58.2.1.3", {"start": v(-54.77, 18.26) * mm, "end": v(-54.77, 8.73) * mm});
            skLineSegment(sketch, "E58.2.2.0", {"start": v(-54.77, -2.38) * mm, "end": v(-45.24, -2.38) * mm});
            skLineSegment(sketch, "E58.2.2.1", {"start": v(-54.77, 7.14) * mm, "end": v(-45.24, 7.14) * mm});
            skLineSegment(sketch, "E58.2.2.2", {"start": v(-45.24, 7.14) * mm, "end": v(-45.24, -2.38) * mm});
            skLineSegment(sketch, "E58.2.2.3", {"start": v(-54.77, 7.14) * mm, "end": v(-54.77, -2.38) * mm});
            skLineSegment(sketch, "E58.2.3.0", {"start": v(-54.77, -13.5) * mm, "end": v(-45.24, -13.5) * mm});
            skLineSegment(sketch, "E58.2.3.1", {"start": v(-54.77, -3.97) * mm, "end": v(-45.24, -3.97) * mm});
            skLineSegment(sketch, "E58.2.3.2", {"start": v(-45.24, -3.97) * mm, "end": v(-45.24, -13.5) * mm});
            skLineSegment(sketch, "E58.2.3.3", {"start": v(-54.77, -3.97) * mm, "end": v(-54.77, -13.5) * mm});
            skLineSegment(sketch, "E58.2.4.0", {"start": v(-54.77, -24.6) * mm, "end": v(-45.24, -24.6) * mm});
            skLineSegment(sketch, "E58.2.4.1", {"start": v(-54.77, -15.08) * mm, "end": v(-45.24, -15.08) * mm});
            skLineSegment(sketch, "E58.2.4.2", {"start": v(-45.24, -15.08) * mm, "end": v(-45.24, -24.6) * mm});
            skLineSegment(sketch, "E58.2.4.3", {"start": v(-54.77, -15.08) * mm, "end": v(-54.77, -24.6) * mm});
            skLineSegment(sketch, "E58.2.5.0", {"start": v(-54.77, -35.72) * mm, "end": v(-45.24, -35.72) * mm});
            skLineSegment(sketch, "E58.2.5.1", {"start": v(-54.77, -26.2) * mm, "end": v(-45.24, -26.2) * mm});
            skLineSegment(sketch, "E58.2.5.2", {"start": v(-45.24, -26.2) * mm, "end": v(-45.24, -35.72) * mm});
            skLineSegment(sketch, "E58.2.5.3", {"start": v(-54.77, -26.2) * mm, "end": v(-54.77, -35.72) * mm});
            skLineSegment(sketch, "E58.3.0.0", {"start": v(-43.66, 19.84) * mm, "end": v(-34.13, 19.84) * mm});
            skLineSegment(sketch, "E58.3.0.1", {"start": v(-43.66, 29.37) * mm, "end": v(-34.13, 29.37) * mm});
            skLineSegment(sketch, "E58.3.0.2", {"start": v(-34.13, 29.37) * mm, "end": v(-34.13, 19.84) * mm});
            skLineSegment(sketch, "E58.3.0.3", {"start": v(-43.66, 29.37) * mm, "end": v(-43.66, 19.84) * mm});
            skLineSegment(sketch, "E58.3.1.0", {"start": v(-43.66, 8.73) * mm, "end": v(-34.13, 8.73) * mm});
            skLineSegment(sketch, "E58.3.1.1", {"start": v(-43.66, 18.26) * mm, "end": v(-34.13, 18.26) * mm});
            skLineSegment(sketch, "E58.3.1.2", {"start": v(-34.13, 18.26) * mm, "end": v(-34.13, 8.73) * mm});
            skLineSegment(sketch, "E58.3.1.3", {"start": v(-43.66, 18.26) * mm, "end": v(-43.66, 8.73) * mm});
            skLineSegment(sketch, "E58.3.2.0", {"start": v(-43.66, -2.38) * mm, "end": v(-34.13, -2.38) * mm});
            skLineSegment(sketch, "E58.3.2.1", {"start": v(-43.66, 7.14) * mm, "end": v(-34.13, 7.14) * mm});
            skLineSegment(sketch, "E58.3.2.2", {"start": v(-34.13, 7.14) * mm, "end": v(-34.13, -2.38) * mm});
            skLineSegment(sketch, "E58.3.2.3", {"start": v(-43.66, 7.14) * mm, "end": v(-43.66, -2.38) * mm});
            skLineSegment(sketch, "E58.3.3.0", {"start": v(-43.66, -13.5) * mm, "end": v(-34.13, -13.5) * mm});
            skLineSegment(sketch, "E58.3.3.1", {"start": v(-43.66, -3.97) * mm, "end": v(-34.13, -3.97) * mm});
            skLineSegment(sketch, "E58.3.3.2", {"start": v(-34.13, -3.97) * mm, "end": v(-34.13, -13.5) * mm});
            skLineSegment(sketch, "E58.3.3.3", {"start": v(-43.66, -3.97) * mm, "end": v(-43.66, -13.5) * mm});
            skLineSegment(sketch, "E58.3.4.0", {"start": v(-43.66, -24.6) * mm, "end": v(-34.13, -24.6) * mm});
            skLineSegment(sketch, "E58.3.4.1", {"start": v(-43.66, -15.08) * mm, "end": v(-34.13, -15.08) * mm});
            skLineSegment(sketch, "E58.3.4.2", {"start": v(-34.13, -15.08) * mm, "end": v(-34.13, -24.6) * mm});
            skLineSegment(sketch, "E58.3.4.3", {"start": v(-43.66, -15.08) * mm, "end": v(-43.66, -24.6) * mm});
            skLineSegment(sketch, "E58.3.5.0", {"start": v(-43.66, -35.72) * mm, "end": v(-34.13, -35.72) * mm});
            skLineSegment(sketch, "E58.3.5.1", {"start": v(-43.66, -26.2) * mm, "end": v(-34.13, -26.2) * mm});
            skLineSegment(sketch, "E58.3.5.2", {"start": v(-34.13, -26.2) * mm, "end": v(-34.13, -35.72) * mm});
            skLineSegment(sketch, "E58.3.5.3", {"start": v(-43.66, -26.2) * mm, "end": v(-43.66, -35.72) * mm});
            skLineSegment(sketch, "E58.4.0.0", {"start": v(-32.54, 19.84) * mm, "end": v(-23.02, 19.84) * mm});
            skLineSegment(sketch, "E58.4.0.1", {"start": v(-32.54, 29.37) * mm, "end": v(-23.02, 29.37) * mm});
            skLineSegment(sketch, "E58.4.0.2", {"start": v(-23.02, 29.37) * mm, "end": v(-23.02, 19.84) * mm});
            skLineSegment(sketch, "E58.4.0.3", {"start": v(-32.54, 29.37) * mm, "end": v(-32.54, 19.84) * mm});
            skLineSegment(sketch, "E58.4.1.0", {"start": v(-32.54, 8.73) * mm, "end": v(-23.02, 8.73) * mm});
            skLineSegment(sketch, "E58.4.1.1", {"start": v(-32.54, 18.26) * mm, "end": v(-23.02, 18.26) * mm});
            skLineSegment(sketch, "E58.4.1.2", {"start": v(-23.02, 18.26) * mm, "end": v(-23.02, 8.73) * mm});
            skLineSegment(sketch, "E58.4.1.3", {"start": v(-32.54, 18.26) * mm, "end": v(-32.54, 8.73) * mm});
            skLineSegment(sketch, "E58.4.2.0", {"start": v(-32.54, -2.38) * mm, "end": v(-23.02, -2.38) * mm});
            skLineSegment(sketch, "E58.4.2.1", {"start": v(-32.54, 7.14) * mm, "end": v(-23.02, 7.14) * mm});
            skLineSegment(sketch, "E58.4.2.2", {"start": v(-23.02, 7.14) * mm, "end": v(-23.02, -2.38) * mm});
            skLineSegment(sketch, "E58.4.2.3", {"start": v(-32.54, 7.14) * mm, "end": v(-32.54, -2.38) * mm});
            skLineSegment(sketch, "E58.4.3.0", {"start": v(-32.54, -13.5) * mm, "end": v(-23.02, -13.5) * mm});
            skLineSegment(sketch, "E58.4.3.1", {"start": v(-32.54, -3.97) * mm, "end": v(-23.02, -3.97) * mm});
            skLineSegment(sketch, "E58.4.3.2", {"start": v(-23.02, -3.97) * mm, "end": v(-23.02, -13.5) * mm});
            skLineSegment(sketch, "E58.4.3.3", {"start": v(-32.54, -3.97) * mm, "end": v(-32.54, -13.5) * mm});
            skLineSegment(sketch, "E58.4.4.0", {"start": v(-32.54, -24.6) * mm, "end": v(-23.02, -24.6) * mm});
            skLineSegment(sketch, "E58.4.4.1", {"start": v(-32.54, -15.08) * mm, "end": v(-23.02, -15.08) * mm});
            skLineSegment(sketch, "E58.4.4.2", {"start": v(-23.02, -15.08) * mm, "end": v(-23.02, -24.6) * mm});
            skLineSegment(sketch, "E58.4.4.3", {"start": v(-32.54, -15.08) * mm, "end": v(-32.54, -24.6) * mm});
            skLineSegment(sketch, "E58.4.5.0", {"start": v(-32.54, -35.72) * mm, "end": v(-23.02, -35.72) * mm});
            skLineSegment(sketch, "E58.4.5.1", {"start": v(-32.54, -26.2) * mm, "end": v(-23.02, -26.2) * mm});
            skLineSegment(sketch, "E58.4.5.2", {"start": v(-23.02, -26.2) * mm, "end": v(-23.02, -35.72) * mm});
            skLineSegment(sketch, "E58.4.5.3", {"start": v(-32.54, -26.2) * mm, "end": v(-32.54, -35.72) * mm});
            skLineSegment(sketch, "E58.5.0.0", {"start": v(-21.43, 19.84) * mm, "end": v(-11.9, 19.84) * mm});
            skLineSegment(sketch, "E58.5.0.1", {"start": v(-21.43, 29.37) * mm, "end": v(-11.9, 29.37) * mm});
            skLineSegment(sketch, "E58.5.0.2", {"start": v(-11.9, 29.37) * mm, "end": v(-11.9, 19.84) * mm});
            skLineSegment(sketch, "E58.5.0.3", {"start": v(-21.43, 29.37) * mm, "end": v(-21.43, 19.84) * mm});
            skLineSegment(sketch, "E58.5.1.0", {"start": v(-21.43, 8.73) * mm, "end": v(-11.9, 8.73) * mm});
            skLineSegment(sketch, "E58.5.1.1", {"start": v(-21.43, 18.26) * mm, "end": v(-11.9, 18.26) * mm});
            skLineSegment(sketch, "E58.5.1.2", {"start": v(-11.9, 18.26) * mm, "end": v(-11.9, 8.73) * mm});
            skLineSegment(sketch, "E58.5.1.3", {"start": v(-21.43, 18.26) * mm, "end": v(-21.43, 8.73) * mm});
            skLineSegment(sketch, "E58.5.2.0", {"start": v(-21.43, -2.38) * mm, "end": v(-11.9, -2.38) * mm});
            skLineSegment(sketch, "E58.5.2.1", {"start": v(-21.43, 7.14) * mm, "end": v(-11.9, 7.14) * mm});
            skLineSegment(sketch, "E58.5.2.2", {"start": v(-11.9, 7.14) * mm, "end": v(-11.9, -2.38) * mm});
            skLineSegment(sketch, "E58.5.2.3", {"start": v(-21.43, 7.14) * mm, "end": v(-21.43, -2.38) * mm});
            skLineSegment(sketch, "E58.5.3.0", {"start": v(-21.43, -13.5) * mm, "end": v(-11.9, -13.5) * mm});
            skLineSegment(sketch, "E58.5.3.1", {"start": v(-21.43, -3.97) * mm, "end": v(-11.9, -3.97) * mm});
            skLineSegment(sketch, "E58.5.3.2", {"start": v(-11.9, -3.97) * mm, "end": v(-11.9, -13.5) * mm});
            skLineSegment(sketch, "E58.5.3.3", {"start": v(-21.43, -3.97) * mm, "end": v(-21.43, -13.5) * mm});
            skLineSegment(sketch, "E58.5.4.0", {"start": v(-21.43, -24.6) * mm, "end": v(-11.9, -24.6) * mm});
            skLineSegment(sketch, "E58.5.4.1", {"start": v(-21.43, -15.08) * mm, "end": v(-11.9, -15.08) * mm});
            skLineSegment(sketch, "E58.5.4.2", {"start": v(-11.9, -15.08) * mm, "end": v(-11.9, -24.6) * mm});
            skLineSegment(sketch, "E58.5.4.3", {"start": v(-21.43, -15.08) * mm, "end": v(-21.43, -24.6) * mm});
            skLineSegment(sketch, "E58.5.5.0", {"start": v(-21.43, -35.72) * mm, "end": v(-11.9, -35.72) * mm});
            skLineSegment(sketch, "E58.5.5.1", {"start": v(-21.43, -26.2) * mm, "end": v(-11.9, -26.2) * mm});
            skLineSegment(sketch, "E58.5.5.2", {"start": v(-11.9, -26.2) * mm, "end": v(-11.9, -35.72) * mm});
            skLineSegment(sketch, "E58.5.5.3", {"start": v(-21.43, -26.2) * mm, "end": v(-21.43, -35.72) * mm});
            skLineSegment(sketch, "E58.6.0.0", {"start": v(-10.32, 19.84) * mm, "end": v(-0.8, 19.84) * mm});
            skLineSegment(sketch, "E58.6.0.1", {"start": v(-10.32, 29.37) * mm, "end": v(-0.8, 29.37) * mm});
            skLineSegment(sketch, "E58.6.0.2", {"start": v(-0.8, 29.37) * mm, "end": v(-0.8, 19.84) * mm});
            skLineSegment(sketch, "E58.6.0.3", {"start": v(-10.32, 29.37) * mm, "end": v(-10.32, 19.84) * mm});
            skLineSegment(sketch, "E58.6.1.0", {"start": v(-10.32, 8.73) * mm, "end": v(-0.8, 8.73) * mm});
            skLineSegment(sketch, "E58.6.1.1", {"start": v(-10.32, 18.26) * mm, "end": v(-0.8, 18.26) * mm});
            skLineSegment(sketch, "E58.6.1.2", {"start": v(-0.8, 18.26) * mm, "end": v(-0.8, 8.73) * mm});
            skLineSegment(sketch, "E58.6.1.3", {"start": v(-10.32, 18.26) * mm, "end": v(-10.32, 8.73) * mm});
            skLineSegment(sketch, "E58.6.2.0", {"start": v(-10.32, -2.38) * mm, "end": v(-0.8, -2.38) * mm});
            skLineSegment(sketch, "E58.6.2.1", {"start": v(-10.32, 7.14) * mm, "end": v(-0.8, 7.14) * mm});
            skLineSegment(sketch, "E58.6.2.2", {"start": v(-0.8, 7.14) * mm, "end": v(-0.8, -2.38) * mm});
            skLineSegment(sketch, "E58.6.2.3", {"start": v(-10.32, 7.14) * mm, "end": v(-10.32, -2.38) * mm});
            skLineSegment(sketch, "E58.6.3.0", {"start": v(-10.32, -13.5) * mm, "end": v(-0.8, -13.5) * mm});
            skLineSegment(sketch, "E58.6.3.1", {"start": v(-10.32, -3.97) * mm, "end": v(-0.8, -3.97) * mm});
            skLineSegment(sketch, "E58.6.3.2", {"start": v(-0.8, -3.97) * mm, "end": v(-0.8, -13.5) * mm});
            skLineSegment(sketch, "E58.6.3.3", {"start": v(-10.32, -3.97) * mm, "end": v(-10.32, -13.5) * mm});
            skLineSegment(sketch, "E58.6.4.0", {"start": v(-10.32, -24.6) * mm, "end": v(-0.8, -24.6) * mm});
            skLineSegment(sketch, "E58.6.4.1", {"start": v(-10.32, -15.08) * mm, "end": v(-0.8, -15.08) * mm});
            skLineSegment(sketch, "E58.6.4.2", {"start": v(-0.8, -15.08) * mm, "end": v(-0.8, -24.6) * mm});
            skLineSegment(sketch, "E58.6.4.3", {"start": v(-10.32, -15.08) * mm, "end": v(-10.32, -24.6) * mm});
            skLineSegment(sketch, "E58.6.5.0", {"start": v(-10.32, -35.72) * mm, "end": v(-0.8, -35.72) * mm});
            skLineSegment(sketch, "E58.6.5.1", {"start": v(-10.32, -26.2) * mm, "end": v(-0.8, -26.2) * mm});
            skLineSegment(sketch, "E58.6.5.2", {"start": v(-0.8, -26.2) * mm, "end": v(-0.8, -35.72) * mm});
            skLineSegment(sketch, "E58.6.5.3", {"start": v(-10.32, -26.2) * mm, "end": v(-10.32, -35.72) * mm});
            skLineSegment(sketch, "E58.7.0.0", {"start": v(0.8, 19.84) * mm, "end": v(10.32, 19.84) * mm});
            skLineSegment(sketch, "E58.7.0.1", {"start": v(0.8, 29.37) * mm, "end": v(10.32, 29.37) * mm});
            skLineSegment(sketch, "E58.7.0.2", {"start": v(10.32, 29.37) * mm, "end": v(10.32, 19.84) * mm});
            skLineSegment(sketch, "E58.7.0.3", {"start": v(0.8, 29.37) * mm, "end": v(0.8, 19.84) * mm});
            skLineSegment(sketch, "E58.7.1.0", {"start": v(0.8, 8.73) * mm, "end": v(10.32, 8.73) * mm});
            skLineSegment(sketch, "E58.7.1.1", {"start": v(0.8, 18.26) * mm, "end": v(10.32, 18.26) * mm});
            skLineSegment(sketch, "E58.7.1.2", {"start": v(10.32, 18.26) * mm, "end": v(10.32, 8.73) * mm});
            skLineSegment(sketch, "E58.7.1.3", {"start": v(0.8, 18.26) * mm, "end": v(0.8, 8.73) * mm});
            skLineSegment(sketch, "E58.7.2.0", {"start": v(0.8, -2.38) * mm, "end": v(10.32, -2.38) * mm});
            skLineSegment(sketch, "E58.7.2.1", {"start": v(0.8, 7.14) * mm, "end": v(10.32, 7.14) * mm});
            skLineSegment(sketch, "E58.7.2.2", {"start": v(10.32, 7.14) * mm, "end": v(10.32, -2.38) * mm});
            skLineSegment(sketch, "E58.7.2.3", {"start": v(0.8, 7.14) * mm, "end": v(0.8, -2.38) * mm});
            skLineSegment(sketch, "E58.7.3.0", {"start": v(0.8, -13.5) * mm, "end": v(10.32, -13.5) * mm});
            skLineSegment(sketch, "E58.7.3.1", {"start": v(0.8, -3.97) * mm, "end": v(10.32, -3.97) * mm});
            skLineSegment(sketch, "E58.7.3.2", {"start": v(10.32, -3.97) * mm, "end": v(10.32, -13.5) * mm});
            skLineSegment(sketch, "E58.7.3.3", {"start": v(0.8, -3.97) * mm, "end": v(0.8, -13.5) * mm});
            skLineSegment(sketch, "E58.7.4.0", {"start": v(0.8, -24.6) * mm, "end": v(10.32, -24.6) * mm});
            skLineSegment(sketch, "E58.7.4.1", {"start": v(0.8, -15.08) * mm, "end": v(10.32, -15.08) * mm});
            skLineSegment(sketch, "E58.7.4.2", {"start": v(10.32, -15.08) * mm, "end": v(10.32, -24.6) * mm});
            skLineSegment(sketch, "E58.7.4.3", {"start": v(0.8, -15.08) * mm, "end": v(0.8, -24.6) * mm});
            skLineSegment(sketch, "E58.7.5.0", {"start": v(0.8, -35.72) * mm, "end": v(10.32, -35.72) * mm});
            skLineSegment(sketch, "E58.7.5.1", {"start": v(0.8, -26.2) * mm, "end": v(10.32, -26.2) * mm});
            skLineSegment(sketch, "E58.7.5.2", {"start": v(10.32, -26.2) * mm, "end": v(10.32, -35.72) * mm});
            skLineSegment(sketch, "E58.7.5.3", {"start": v(0.8, -26.2) * mm, "end": v(0.8, -35.72) * mm});
            skLineSegment(sketch, "E58.8.0.0", {"start": v(11.9, 19.84) * mm, "end": v(21.43, 19.84) * mm});
            skLineSegment(sketch, "E58.8.0.1", {"start": v(11.9, 29.37) * mm, "end": v(21.43, 29.37) * mm});
            skLineSegment(sketch, "E58.8.0.2", {"start": v(21.43, 29.37) * mm, "end": v(21.43, 19.84) * mm});
            skLineSegment(sketch, "E58.8.0.3", {"start": v(11.9, 29.37) * mm, "end": v(11.9, 19.84) * mm});
            skLineSegment(sketch, "E58.8.1.0", {"start": v(11.9, 8.73) * mm, "end": v(21.43, 8.73) * mm});
            skLineSegment(sketch, "E58.8.1.1", {"start": v(11.9, 18.26) * mm, "end": v(21.43, 18.26) * mm});
            skLineSegment(sketch, "E58.8.1.2", {"start": v(21.43, 18.26) * mm, "end": v(21.43, 8.73) * mm});
            skLineSegment(sketch, "E58.8.1.3", {"start": v(11.9, 18.26) * mm, "end": v(11.9, 8.73) * mm});
            skLineSegment(sketch, "E58.8.2.0", {"start": v(11.9, -2.38) * mm, "end": v(21.43, -2.38) * mm});
            skLineSegment(sketch, "E58.8.2.1", {"start": v(11.9, 7.14) * mm, "end": v(21.43, 7.14) * mm});
            skLineSegment(sketch, "E58.8.2.2", {"start": v(21.43, 7.14) * mm, "end": v(21.43, -2.38) * mm});
            skLineSegment(sketch, "E58.8.2.3", {"start": v(11.9, 7.14) * mm, "end": v(11.9, -2.38) * mm});
            skLineSegment(sketch, "E58.8.3.0", {"start": v(11.9, -13.5) * mm, "end": v(21.43, -13.5) * mm});
            skLineSegment(sketch, "E58.8.3.1", {"start": v(11.9, -3.97) * mm, "end": v(21.43, -3.97) * mm});
            skLineSegment(sketch, "E58.8.3.2", {"start": v(21.43, -3.97) * mm, "end": v(21.43, -13.5) * mm});
            skLineSegment(sketch, "E58.8.3.3", {"start": v(11.9, -3.97) * mm, "end": v(11.9, -13.5) * mm});
            skLineSegment(sketch, "E58.8.4.0", {"start": v(11.9, -24.6) * mm, "end": v(21.43, -24.6) * mm});
            skLineSegment(sketch, "E58.8.4.1", {"start": v(11.9, -15.08) * mm, "end": v(21.43, -15.08) * mm});
            skLineSegment(sketch, "E58.8.4.2", {"start": v(21.43, -15.08) * mm, "end": v(21.43, -24.6) * mm});
            skLineSegment(sketch, "E58.8.4.3", {"start": v(11.9, -15.08) * mm, "end": v(11.9, -24.6) * mm});
            skLineSegment(sketch, "E58.8.5.0", {"start": v(11.9, -35.72) * mm, "end": v(21.43, -35.72) * mm});
            skLineSegment(sketch, "E58.8.5.1", {"start": v(11.9, -26.2) * mm, "end": v(21.43, -26.2) * mm});
            skLineSegment(sketch, "E58.8.5.2", {"start": v(21.43, -26.2) * mm, "end": v(21.43, -35.72) * mm});
            skLineSegment(sketch, "E58.8.5.3", {"start": v(11.9, -26.2) * mm, "end": v(11.9, -35.72) * mm});
            skLineSegment(sketch, "E58.9.0.0", {"start": v(23.02, 19.84) * mm, "end": v(32.54, 19.84) * mm});
            skLineSegment(sketch, "E58.9.0.1", {"start": v(23.02, 29.37) * mm, "end": v(32.54, 29.37) * mm});
            skLineSegment(sketch, "E58.9.0.2", {"start": v(32.54, 29.37) * mm, "end": v(32.54, 19.84) * mm});
            skLineSegment(sketch, "E58.9.0.3", {"start": v(23.02, 29.37) * mm, "end": v(23.02, 19.84) * mm});
            skLineSegment(sketch, "E58.9.1.0", {"start": v(23.02, 8.73) * mm, "end": v(32.54, 8.73) * mm});
            skLineSegment(sketch, "E58.9.1.1", {"start": v(23.02, 18.26) * mm, "end": v(32.54, 18.26) * mm});
            skLineSegment(sketch, "E58.9.1.2", {"start": v(32.54, 18.26) * mm, "end": v(32.54, 8.73) * mm});
            skLineSegment(sketch, "E58.9.1.3", {"start": v(23.02, 18.26) * mm, "end": v(23.02, 8.73) * mm});
            skLineSegment(sketch, "E58.9.2.0", {"start": v(23.02, -2.38) * mm, "end": v(32.54, -2.38) * mm});
            skLineSegment(sketch, "E58.9.2.1", {"start": v(23.02, 7.14) * mm, "end": v(32.54, 7.14) * mm});
            skLineSegment(sketch, "E58.9.2.2", {"start": v(32.54, 7.14) * mm, "end": v(32.54, -2.38) * mm});
            skLineSegment(sketch, "E58.9.2.3", {"start": v(23.02, 7.14) * mm, "end": v(23.02, -2.38) * mm});
            skLineSegment(sketch, "E58.9.3.0", {"start": v(23.02, -13.5) * mm, "end": v(32.54, -13.5) * mm});
            skLineSegment(sketch, "E58.9.3.1", {"start": v(23.02, -3.97) * mm, "end": v(32.54, -3.97) * mm});
            skLineSegment(sketch, "E58.9.3.2", {"start": v(32.54, -3.97) * mm, "end": v(32.54, -13.5) * mm});
            skLineSegment(sketch, "E58.9.3.3", {"start": v(23.02, -3.97) * mm, "end": v(23.02, -13.5) * mm});
            skLineSegment(sketch, "E58.9.4.0", {"start": v(23.02, -24.6) * mm, "end": v(32.54, -24.6) * mm});
            skLineSegment(sketch, "E58.9.4.1", {"start": v(23.02, -15.08) * mm, "end": v(32.54, -15.08) * mm});
            skLineSegment(sketch, "E58.9.4.2", {"start": v(32.54, -15.08) * mm, "end": v(32.54, -24.6) * mm});
            skLineSegment(sketch, "E58.9.4.3", {"start": v(23.02, -15.08) * mm, "end": v(23.02, -24.6) * mm});
            skLineSegment(sketch, "E58.9.5.0", {"start": v(23.02, -35.72) * mm, "end": v(32.54, -35.72) * mm});
            skLineSegment(sketch, "E58.9.5.1", {"start": v(23.02, -26.2) * mm, "end": v(32.54, -26.2) * mm});
            skLineSegment(sketch, "E58.9.5.2", {"start": v(32.54, -26.2) * mm, "end": v(32.54, -35.72) * mm});
            skLineSegment(sketch, "E58.9.5.3", {"start": v(23.02, -26.2) * mm, "end": v(23.02, -35.72) * mm});
            skLineSegment(sketch, "E58.10.0.0", {"start": v(34.13, 19.84) * mm, "end": v(43.66, 19.84) * mm});
            skLineSegment(sketch, "E58.10.0.1", {"start": v(34.13, 29.37) * mm, "end": v(43.66, 29.37) * mm});
            skLineSegment(sketch, "E58.10.0.2", {"start": v(43.66, 29.37) * mm, "end": v(43.66, 19.84) * mm});
            skLineSegment(sketch, "E58.10.0.3", {"start": v(34.13, 29.37) * mm, "end": v(34.13, 19.84) * mm});
            skLineSegment(sketch, "E58.10.1.0", {"start": v(34.13, 8.73) * mm, "end": v(43.66, 8.73) * mm});
            skLineSegment(sketch, "E58.10.1.1", {"start": v(34.13, 18.26) * mm, "end": v(43.66, 18.26) * mm});
            skLineSegment(sketch, "E58.10.1.2", {"start": v(43.66, 18.26) * mm, "end": v(43.66, 8.73) * mm});
            skLineSegment(sketch, "E58.10.1.3", {"start": v(34.13, 18.26) * mm, "end": v(34.13, 8.73) * mm});
            skLineSegment(sketch, "E58.10.2.0", {"start": v(34.13, -2.38) * mm, "end": v(43.66, -2.38) * mm});
            skLineSegment(sketch, "E58.10.2.1", {"start": v(34.13, 7.14) * mm, "end": v(43.66, 7.14) * mm});
            skLineSegment(sketch, "E58.10.2.2", {"start": v(43.66, 7.14) * mm, "end": v(43.66, -2.38) * mm});
            skLineSegment(sketch, "E58.10.2.3", {"start": v(34.13, 7.14) * mm, "end": v(34.13, -2.38) * mm});
            skLineSegment(sketch, "E58.10.3.0", {"start": v(34.13, -13.5) * mm, "end": v(43.66, -13.5) * mm});
            skLineSegment(sketch, "E58.10.3.1", {"start": v(34.13, -3.97) * mm, "end": v(43.66, -3.97) * mm});
            skLineSegment(sketch, "E58.10.3.2", {"start": v(43.66, -3.97) * mm, "end": v(43.66, -13.5) * mm});
            skLineSegment(sketch, "E58.10.3.3", {"start": v(34.13, -3.97) * mm, "end": v(34.13, -13.5) * mm});
            skLineSegment(sketch, "E58.10.4.0", {"start": v(34.13, -24.6) * mm, "end": v(43.66, -24.6) * mm});
            skLineSegment(sketch, "E58.10.4.1", {"start": v(34.13, -15.08) * mm, "end": v(43.66, -15.08) * mm});
            skLineSegment(sketch, "E58.10.4.2", {"start": v(43.66, -15.08) * mm, "end": v(43.66, -24.6) * mm});
            skLineSegment(sketch, "E58.10.4.3", {"start": v(34.13, -15.08) * mm, "end": v(34.13, -24.6) * mm});
            skLineSegment(sketch, "E58.10.5.0", {"start": v(34.13, -35.72) * mm, "end": v(43.66, -35.72) * mm});
            skLineSegment(sketch, "E58.10.5.1", {"start": v(34.13, -26.2) * mm, "end": v(43.66, -26.2) * mm});
            skLineSegment(sketch, "E58.10.5.2", {"start": v(43.66, -26.2) * mm, "end": v(43.66, -35.72) * mm});
            skLineSegment(sketch, "E58.10.5.3", {"start": v(34.13, -26.2) * mm, "end": v(34.13, -35.72) * mm});
            skLineSegment(sketch, "E58.11.0.0", {"start": v(45.24, 19.84) * mm, "end": v(54.77, 19.84) * mm});
            skLineSegment(sketch, "E58.11.0.1", {"start": v(45.24, 29.37) * mm, "end": v(54.77, 29.37) * mm});
            skLineSegment(sketch, "E58.11.0.2", {"start": v(54.77, 29.37) * mm, "end": v(54.77, 19.84) * mm});
            skLineSegment(sketch, "E58.11.0.3", {"start": v(45.24, 29.37) * mm, "end": v(45.24, 19.84) * mm});
            skLineSegment(sketch, "E58.11.1.0", {"start": v(45.24, 8.73) * mm, "end": v(54.77, 8.73) * mm});
            skLineSegment(sketch, "E58.11.1.1", {"start": v(45.24, 18.26) * mm, "end": v(54.77, 18.26) * mm});
            skLineSegment(sketch, "E58.11.1.2", {"start": v(54.77, 18.26) * mm, "end": v(54.77, 8.73) * mm});
            skLineSegment(sketch, "E58.11.1.3", {"start": v(45.24, 18.26) * mm, "end": v(45.24, 8.73) * mm});
            skLineSegment(sketch, "E58.11.2.0", {"start": v(45.24, -2.38) * mm, "end": v(54.77, -2.38) * mm});
            skLineSegment(sketch, "E58.11.2.1", {"start": v(45.24, 7.14) * mm, "end": v(54.77, 7.14) * mm});
            skLineSegment(sketch, "E58.11.2.2", {"start": v(54.77, 7.14) * mm, "end": v(54.77, -2.38) * mm});
            skLineSegment(sketch, "E58.11.2.3", {"start": v(45.24, 7.14) * mm, "end": v(45.24, -2.38) * mm});
            skLineSegment(sketch, "E58.11.3.0", {"start": v(45.24, -13.5) * mm, "end": v(54.77, -13.5) * mm});
            skLineSegment(sketch, "E58.11.3.1", {"start": v(45.24, -3.97) * mm, "end": v(54.77, -3.97) * mm});
            skLineSegment(sketch, "E58.11.3.2", {"start": v(54.77, -3.97) * mm, "end": v(54.77, -13.5) * mm});
            skLineSegment(sketch, "E58.11.3.3", {"start": v(45.24, -3.97) * mm, "end": v(45.24, -13.5) * mm});
            skLineSegment(sketch, "E58.11.4.0", {"start": v(45.24, -24.6) * mm, "end": v(54.77, -24.6) * mm});
            skLineSegment(sketch, "E58.11.4.1", {"start": v(45.24, -15.08) * mm, "end": v(54.77, -15.08) * mm});
            skLineSegment(sketch, "E58.11.4.2", {"start": v(54.77, -15.08) * mm, "end": v(54.77, -24.6) * mm});
            skLineSegment(sketch, "E58.11.4.3", {"start": v(45.24, -15.08) * mm, "end": v(45.24, -24.6) * mm});
            skLineSegment(sketch, "E58.11.5.0", {"start": v(45.24, -35.72) * mm, "end": v(54.77, -35.72) * mm});
            skLineSegment(sketch, "E58.11.5.1", {"start": v(45.24, -26.2) * mm, "end": v(54.77, -26.2) * mm});
            skLineSegment(sketch, "E58.11.5.2", {"start": v(54.77, -26.2) * mm, "end": v(54.77, -35.72) * mm});
            skLineSegment(sketch, "E58.11.5.3", {"start": v(45.24, -26.2) * mm, "end": v(45.24, -35.72) * mm});
            skLineSegment(sketch, "E58.12.0.0", {"start": v(56.36, 19.84) * mm, "end": v(65.88, 19.84) * mm});
            skLineSegment(sketch, "E58.12.0.1", {"start": v(56.36, 29.37) * mm, "end": v(65.88, 29.37) * mm});
            skLineSegment(sketch, "E58.12.0.2", {"start": v(65.88, 29.37) * mm, "end": v(65.88, 19.84) * mm});
            skLineSegment(sketch, "E58.12.0.3", {"start": v(56.36, 29.37) * mm, "end": v(56.36, 19.84) * mm});
            skLineSegment(sketch, "E58.12.1.0", {"start": v(56.36, 8.73) * mm, "end": v(65.88, 8.73) * mm});
            skLineSegment(sketch, "E58.12.1.1", {"start": v(56.36, 18.26) * mm, "end": v(65.88, 18.26) * mm});
            skLineSegment(sketch, "E58.12.1.2", {"start": v(65.88, 18.26) * mm, "end": v(65.88, 8.73) * mm});
            skLineSegment(sketch, "E58.12.1.3", {"start": v(56.36, 18.26) * mm, "end": v(56.36, 8.73) * mm});
            skLineSegment(sketch, "E58.12.2.0", {"start": v(56.36, -2.38) * mm, "end": v(65.88, -2.38) * mm});
            skLineSegment(sketch, "E58.12.2.1", {"start": v(56.36, 7.14) * mm, "end": v(65.88, 7.14) * mm});
            skLineSegment(sketch, "E58.12.2.2", {"start": v(65.88, 7.14) * mm, "end": v(65.88, -2.38) * mm});
            skLineSegment(sketch, "E58.12.2.3", {"start": v(56.36, 7.14) * mm, "end": v(56.36, -2.38) * mm});
            skLineSegment(sketch, "E58.12.3.0", {"start": v(56.36, -13.5) * mm, "end": v(65.88, -13.5) * mm});
            skLineSegment(sketch, "E58.12.3.1", {"start": v(56.36, -3.97) * mm, "end": v(65.88, -3.97) * mm});
            skLineSegment(sketch, "E58.12.3.2", {"start": v(65.88, -3.97) * mm, "end": v(65.88, -13.5) * mm});
            skLineSegment(sketch, "E58.12.3.3", {"start": v(56.36, -3.97) * mm, "end": v(56.36, -13.5) * mm});
            skLineSegment(sketch, "E58.12.4.0", {"start": v(56.36, -24.6) * mm, "end": v(65.88, -24.6) * mm});
            skLineSegment(sketch, "E58.12.4.1", {"start": v(56.36, -15.08) * mm, "end": v(65.88, -15.08) * mm});
            skLineSegment(sketch, "E58.12.4.2", {"start": v(65.88, -15.08) * mm, "end": v(65.88, -24.6) * mm});
            skLineSegment(sketch, "E58.12.4.3", {"start": v(56.36, -15.08) * mm, "end": v(56.36, -24.6) * mm});
            skLineSegment(sketch, "E58.12.5.0", {"start": v(56.36, -35.72) * mm, "end": v(65.88, -35.72) * mm});
            skLineSegment(sketch, "E58.12.5.1", {"start": v(56.36, -26.2) * mm, "end": v(65.88, -26.2) * mm});
            skLineSegment(sketch, "E58.12.5.2", {"start": v(65.88, -26.2) * mm, "end": v(65.88, -35.72) * mm});
            skLineSegment(sketch, "E58.12.5.3", {"start": v(56.36, -26.2) * mm, "end": v(56.36, -35.72) * mm});
            skLineSegment(sketch, "E58.13.0.0", {"start": v(67.47, 19.84) * mm, "end": v(77, 19.84) * mm});
            skLineSegment(sketch, "E58.13.0.1", {"start": v(67.47, 29.37) * mm, "end": v(77, 29.37) * mm});
            skLineSegment(sketch, "E58.13.0.2", {"start": v(77, 29.37) * mm, "end": v(77, 19.84) * mm});
            skLineSegment(sketch, "E58.13.0.3", {"start": v(67.47, 29.37) * mm, "end": v(67.47, 19.84) * mm});
            skLineSegment(sketch, "E58.13.1.0", {"start": v(67.47, 8.73) * mm, "end": v(77, 8.73) * mm});
            skLineSegment(sketch, "E58.13.1.1", {"start": v(67.47, 18.26) * mm, "end": v(77, 18.26) * mm});
            skLineSegment(sketch, "E58.13.1.2", {"start": v(77, 18.26) * mm, "end": v(77, 8.73) * mm});
            skLineSegment(sketch, "E58.13.1.3", {"start": v(67.47, 18.26) * mm, "end": v(67.47, 8.73) * mm});
            skLineSegment(sketch, "E58.13.2.0", {"start": v(67.47, -2.38) * mm, "end": v(77, -2.38) * mm});
            skLineSegment(sketch, "E58.13.2.1", {"start": v(67.47, 7.14) * mm, "end": v(77, 7.14) * mm});
            skLineSegment(sketch, "E58.13.2.2", {"start": v(77, 7.14) * mm, "end": v(77, -2.38) * mm});
            skLineSegment(sketch, "E58.13.2.3", {"start": v(67.47, 7.14) * mm, "end": v(67.47, -2.38) * mm});
            skLineSegment(sketch, "E58.13.3.0", {"start": v(67.47, -13.5) * mm, "end": v(77, -13.5) * mm});
            skLineSegment(sketch, "E58.13.3.1", {"start": v(67.47, -3.97) * mm, "end": v(77, -3.97) * mm});
            skLineSegment(sketch, "E58.13.3.2", {"start": v(77, -3.97) * mm, "end": v(77, -13.5) * mm});
            skLineSegment(sketch, "E58.13.3.3", {"start": v(67.47, -3.97) * mm, "end": v(67.47, -13.5) * mm});
            skLineSegment(sketch, "E58.13.4.0", {"start": v(67.47, -24.6) * mm, "end": v(77, -24.6) * mm});
            skLineSegment(sketch, "E58.13.4.1", {"start": v(67.47, -15.08) * mm, "end": v(77, -15.08) * mm});
            skLineSegment(sketch, "E58.13.4.2", {"start": v(77, -15.08) * mm, "end": v(77, -24.6) * mm});
            skLineSegment(sketch, "E58.13.4.3", {"start": v(67.47, -15.08) * mm, "end": v(67.47, -24.6) * mm});
            skLineSegment(sketch, "E58.13.5.0", {"start": v(67.47, -35.72) * mm, "end": v(77, -35.72) * mm});
            skLineSegment(sketch, "E58.13.5.1", {"start": v(67.47, -26.2) * mm, "end": v(77, -26.2) * mm});
            skLineSegment(sketch, "E58.13.5.2", {"start": v(77, -26.2) * mm, "end": v(77, -35.72) * mm});
            skLineSegment(sketch, "E58.13.5.3", {"start": v(67.47, -26.2) * mm, "end": v(67.47, -35.72) * mm});
            skLineSegment(sketch, "E58.direction1", {"start": v(-77, 19.84) * mm, "end": v(-65.88, 19.84) * mm, "construction": true});
            skLineSegment(sketch, "E58.direction2", {"start": v(-77, 19.84) * mm, "end": v(-77, 8.73) * mm, "construction": true});
            skLineSegment(sketch, "E59.bottom", {"start": v(-43.66, -35.72) * mm, "end": v(43.66, -35.72) * mm});
            skLineSegment(sketch, "E59.top", {"start": v(-43.66, -26.2) * mm, "end": v(43.66, -26.2) * mm});
            skLineSegment(sketch, "E59.left", {"start": v(-43.66, -35.72) * mm, "end": v(-43.66, -26.2) * mm});
            skLineSegment(sketch, "E59.right", {"start": v(43.66, -35.72) * mm, "end": v(43.66, -26.2) * mm});
            skLineSegment(sketch, "E60.bottom", {"start": v(-56.36, -24.6) * mm, "end": v(-77, -24.6) * mm});
            skLineSegment(sketch, "E60.top", {"start": v(-56.36, -15.08) * mm, "end": v(-77, -15.08) * mm});
            skLineSegment(sketch, "E60.left", {"start": v(-56.36, -24.6) * mm, "end": v(-56.36, -15.08) * mm});
            skLineSegment(sketch, "E60.right", {"start": v(-77, -24.6) * mm, "end": v(-77, -15.08) * mm});
            skLineSegment(sketch, "E61.bottom", {"start": v(56.36, -24.6) * mm, "end": v(77, -24.6) * mm});
            skLineSegment(sketch, "E61.top", {"start": v(56.36, -15.08) * mm, "end": v(77, -15.08) * mm});
            skLineSegment(sketch, "E61.left", {"start": v(56.36, -24.6) * mm, "end": v(56.36, -15.08) * mm});
            skLineSegment(sketch, "E61.right", {"start": v(77, -24.6) * mm, "end": v(77, -15.08) * mm});
            skLineSegment(sketch, "E62.bottom", {"start": v(56.36, -13.5) * mm, "end": v(77, -13.5) * mm});
            skLineSegment(sketch, "E62.top", {"start": v(56.36, -3.97) * mm, "end": v(77, -3.97) * mm});
            skLineSegment(sketch, "E62.left", {"start": v(56.36, -13.5) * mm, "end": v(56.36, -3.97) * mm});
            skLineSegment(sketch, "E62.right", {"start": v(77, -13.5) * mm, "end": v(77, -3.97) * mm});
            skLineSegment(sketch, "E63.0.1.0", {"start": v(56.36, -46.83) * mm, "end": v(65.88, -46.83) * mm});
            skLineSegment(sketch, "E63.0.1.1", {"start": v(54.77, -37.3) * mm, "end": v(54.77, -46.83) * mm});
            skLineSegment(sketch, "E63.0.1.2", {"start": v(77, -37.3) * mm, "end": v(77, -46.83) * mm});
            skLineSegment(sketch, "E63.0.1.3", {"start": v(67.47, -37.3) * mm, "end": v(67.47, -46.83) * mm});
            skLineSegment(sketch, "E63.0.1.4", {"start": v(45.24, -37.3) * mm, "end": v(45.24, -46.83) * mm});
            skLineSegment(sketch, "E63.0.1.5", {"start": v(56.36, -37.3) * mm, "end": v(56.36, -46.83) * mm});
            skLineSegment(sketch, "E63.0.1.6", {"start": v(56.36, -37.3) * mm, "end": v(65.88, -37.3) * mm});
            skLineSegment(sketch, "E63.0.1.7", {"start": v(65.88, -37.3) * mm, "end": v(65.88, -46.83) * mm});
            skLineSegment(sketch, "E63.0.1.8", {"start": v(67.47, -46.83) * mm, "end": v(77, -46.83) * mm});
            skLineSegment(sketch, "E63.0.1.9", {"start": v(45.24, -46.83) * mm, "end": v(54.77, -46.83) * mm});
            skLineSegment(sketch, "E63.0.1.10", {"start": v(67.47, -37.3) * mm, "end": v(77, -37.3) * mm});
            skLineSegment(sketch, "E63.0.1.11", {"start": v(45.24, -37.3) * mm, "end": v(54.77, -37.3) * mm});
            skLineSegment(sketch, "E63.direction1", {"start": v(45.24, -35.72) * mm, "end": v(70.64, -35.72) * mm, "construction": true});
            skLineSegment(sketch, "E63.direction2", {"start": v(45.24, -35.72) * mm, "end": v(45.24, -46.83) * mm, "construction": true});
            skLineSegment(sketch, "E64.0.1.0", {"start": v(-65.88, -46.83) * mm, "end": v(-56.36, -46.83) * mm});
            skLineSegment(sketch, "E64.0.1.1", {"start": v(-65.88, -37.3) * mm, "end": v(-56.36, -37.3) * mm});
            skLineSegment(sketch, "E64.0.1.2", {"start": v(-67.47, -37.3) * mm, "end": v(-67.47, -46.83) * mm});
            skLineSegment(sketch, "E64.0.1.3", {"start": v(-45.24, -37.3) * mm, "end": v(-45.24, -46.83) * mm});
            skLineSegment(sketch, "E64.0.1.4", {"start": v(-54.77, -37.3) * mm, "end": v(-45.24, -37.3) * mm});
            skLineSegment(sketch, "E64.0.1.5", {"start": v(-77, -37.3) * mm, "end": v(-67.47, -37.3) * mm});
            skLineSegment(sketch, "E64.0.1.6", {"start": v(-77, -37.3) * mm, "end": v(-77, -46.83) * mm});
            skLineSegment(sketch, "E64.0.1.7", {"start": v(-54.77, -37.3) * mm, "end": v(-54.77, -46.83) * mm});
            skLineSegment(sketch, "E64.0.1.8", {"start": v(-65.88, -37.3) * mm, "end": v(-65.88, -46.83) * mm});
            skLineSegment(sketch, "E64.0.1.9", {"start": v(-56.36, -37.3) * mm, "end": v(-56.36, -46.83) * mm});
            skLineSegment(sketch, "E64.0.1.10", {"start": v(-77, -46.83) * mm, "end": v(-67.47, -46.83) * mm});
            skLineSegment(sketch, "E64.0.1.11", {"start": v(-54.77, -46.83) * mm, "end": v(-45.24, -46.83) * mm});
            skLineSegment(sketch, "E64.direction1", {"start": v(-77, -35.72) * mm, "end": v(-51.6, -35.72) * mm, "construction": true});
            skLineSegment(sketch, "E64.direction2", {"start": v(-77, -35.72) * mm, "end": v(-77, -46.83) * mm, "construction": true});
            skLineSegment(sketch, "E65.bottom", {"start": v(-77, -37.3) * mm, "end": v(-45.24, -37.3) * mm});
            skLineSegment(sketch, "E65.top", {"start": v(-77, -46.83) * mm, "end": v(-45.24, -46.83) * mm});
            skSolve(sketch);
        }
        {
            var Q0;
            Q0 = qSketchRegion(id + "F44", true);
            extrude(context, id + "F45", {"entities" : qUnion([Q0]), "depth" : 4 * mm});
        }
    });
